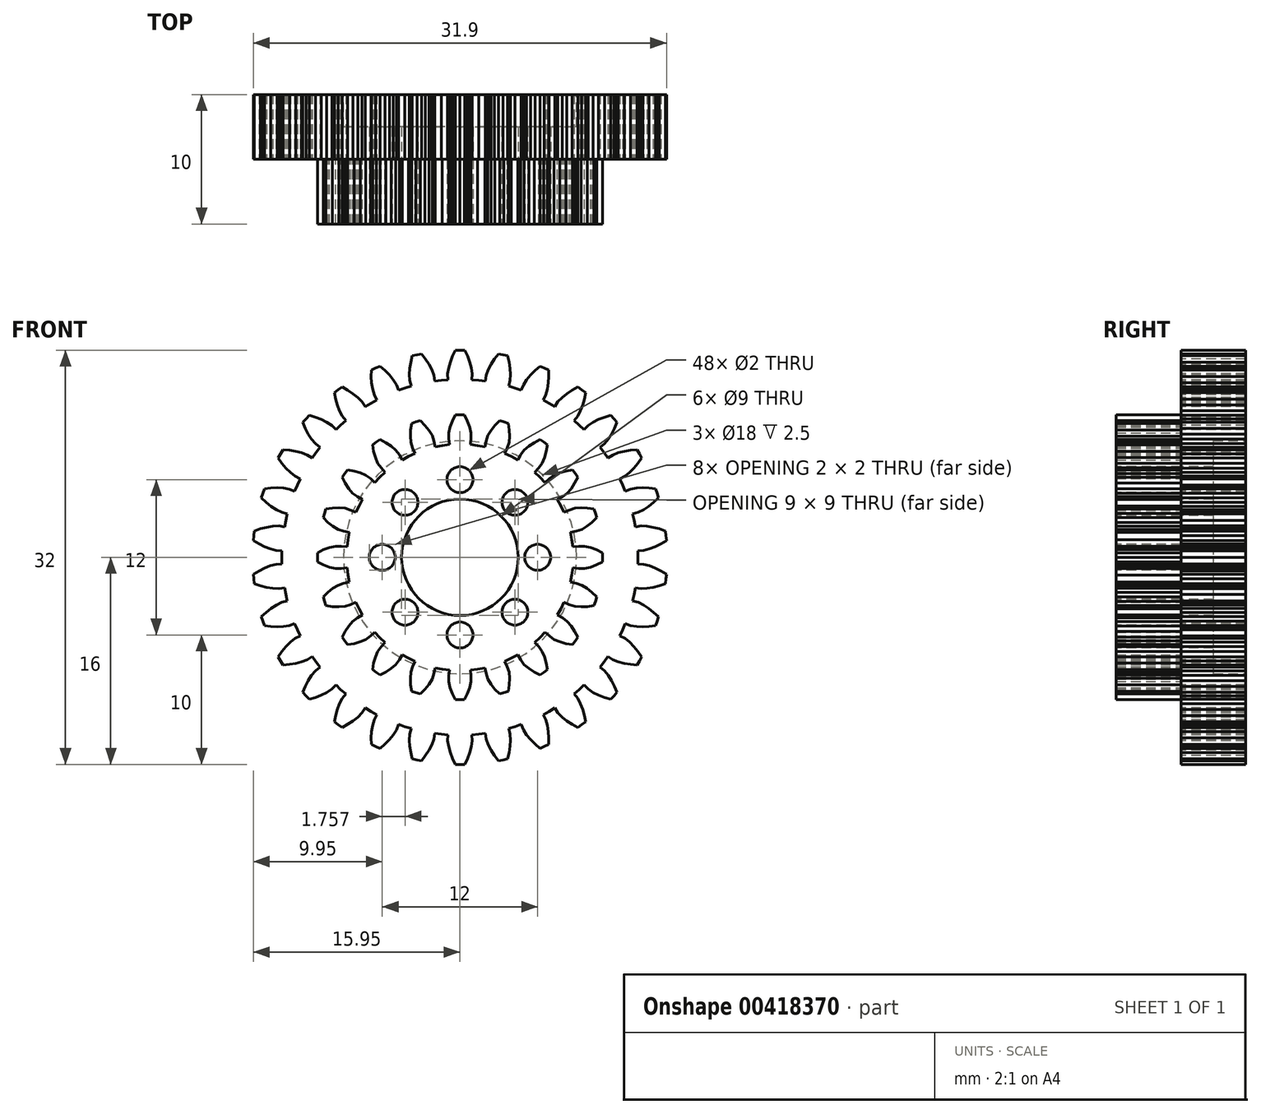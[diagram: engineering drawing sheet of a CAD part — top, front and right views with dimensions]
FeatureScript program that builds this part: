
annotation { "Feature Type Name" : "Feature", "Feature Type Description" : "" }
export const myFeature = defineFeature(function(context is Context, id is Id, definition is map)
    precondition{}
    {
        {
            var Q0;
            Q0=qCreatedBy(makeId("Front.planeOp"),FACE);
            var sketch = newSketch(context, id + "F0", { "sketchPlane" : qUnion([Q0])});
            skLineSegment(sketch, "E0", {"start": v(8.64, -1.37) * mm, "end": v(8.71, -0.82) * mm});
            skLineSegment(sketch, "E1", {"start": v(8.71, -0.82) * mm, "end": v(9.16, -0.86) * mm});
            skLineSegment(sketch, "E2", {"start": v(9.16, -0.86) * mm, "end": v(9.61, -0.86) * mm});
            skLineSegment(sketch, "E3", {"start": v(9.61, -0.86) * mm, "end": v(10.07, -0.75) * mm});
            skLineSegment(sketch, "E4", {"start": v(10.07, -0.75) * mm, "end": v(10.53, -0.58) * mm});
            skLineSegment(sketch, "E5", {"start": v(10.53, -0.58) * mm, "end": v(11, -0.35) * mm});
            skLineSegment(sketch, "E6", {"start": v(11, -0.35) * mm, "end": v(11, 0) * mm});
            skLineSegment(sketch, "E7", {"start": v(11, 0) * mm, "end": v(11, 0.35) * mm});
            skLineSegment(sketch, "E8", {"start": v(11, 0.35) * mm, "end": v(10.53, 0.58) * mm});
            skLineSegment(sketch, "E9", {"start": v(10.53, 0.58) * mm, "end": v(10.07, 0.75) * mm});
            skLineSegment(sketch, "E10", {"start": v(10.07, 0.75) * mm, "end": v(9.61, 0.86) * mm});
            skLineSegment(sketch, "E11", {"start": v(9.61, 0.86) * mm, "end": v(9.16, 0.86) * mm});
            skLineSegment(sketch, "E12", {"start": v(9.16, 0.86) * mm, "end": v(8.71, 0.82) * mm});
            skLineSegment(sketch, "E13", {"start": v(8.71, 0.82) * mm, "end": v(8.64, 1.37) * mm});
            skLineSegment(sketch, "E14", {"start": v(8.64, 1.37) * mm, "end": v(8.54, 1.92) * mm});
            skLineSegment(sketch, "E15", {"start": v(8.54, 1.92) * mm, "end": v(8.98, 2.01) * mm});
            skLineSegment(sketch, "E16", {"start": v(8.98, 2.01) * mm, "end": v(9.4, 2.15) * mm});
            skLineSegment(sketch, "E17", {"start": v(9.4, 2.15) * mm, "end": v(9.81, 2.4) * mm});
            skLineSegment(sketch, "E18", {"start": v(9.81, 2.4) * mm, "end": v(10.2, 2.7) * mm});
            skLineSegment(sketch, "E19", {"start": v(10.2, 2.7) * mm, "end": v(10.56, 3.07) * mm});
            skLineSegment(sketch, "E20", {"start": v(10.56, 3.07) * mm, "end": v(10.46, 3.4) * mm});
            skLineSegment(sketch, "E21", {"start": v(10.46, 3.4) * mm, "end": v(10.35, 3.73) * mm});
            skLineSegment(sketch, "E22", {"start": v(10.35, 3.73) * mm, "end": v(9.84, 3.8) * mm});
            skLineSegment(sketch, "E23", {"start": v(9.84, 3.8) * mm, "end": v(9.35, 3.83) * mm});
            skLineSegment(sketch, "E24", {"start": v(9.35, 3.83) * mm, "end": v(8.88, 3.79) * mm});
            skLineSegment(sketch, "E25", {"start": v(8.88, 3.79) * mm, "end": v(8.45, 3.65) * mm});
            skLineSegment(sketch, "E26", {"start": v(8.45, 3.65) * mm, "end": v(8.03, 3.47) * mm});
            skLineSegment(sketch, "E27", {"start": v(8.03, 3.47) * mm, "end": v(7.8, 3.97) * mm});
            skLineSegment(sketch, "E28", {"start": v(7.8, 3.97) * mm, "end": v(7.53, 4.46) * mm});
            skLineSegment(sketch, "E29", {"start": v(7.53, 4.46) * mm, "end": v(7.92, 4.69) * mm});
            skLineSegment(sketch, "E30", {"start": v(7.92, 4.69) * mm, "end": v(8.28, 4.95) * mm});
            skLineSegment(sketch, "E31", {"start": v(8.28, 4.95) * mm, "end": v(8.6, 5.3) * mm});
            skLineSegment(sketch, "E32", {"start": v(8.6, 5.3) * mm, "end": v(8.86, 5.72) * mm});
            skLineSegment(sketch, "E33", {"start": v(8.86, 5.72) * mm, "end": v(9.1, 6.18) * mm});
            skLineSegment(sketch, "E34", {"start": v(9.1, 6.18) * mm, "end": v(8.9, 6.47) * mm});
            skLineSegment(sketch, "E35", {"start": v(8.9, 6.47) * mm, "end": v(8.7, 6.74) * mm});
            skLineSegment(sketch, "E36", {"start": v(8.7, 6.74) * mm, "end": v(8.18, 6.66) * mm});
            skLineSegment(sketch, "E37", {"start": v(8.18, 6.66) * mm, "end": v(7.7, 6.53) * mm});
            skLineSegment(sketch, "E38", {"start": v(7.7, 6.53) * mm, "end": v(7.27, 6.35) * mm});
            skLineSegment(sketch, "E39", {"start": v(7.27, 6.35) * mm, "end": v(6.9, 6.08) * mm});
            skLineSegment(sketch, "E40", {"start": v(6.9, 6.08) * mm, "end": v(6.57, 5.78) * mm});
            skLineSegment(sketch, "E41", {"start": v(6.57, 5.78) * mm, "end": v(6.19, 6.19) * mm});
            skLineSegment(sketch, "E42", {"start": v(6.19, 6.19) * mm, "end": v(5.78, 6.57) * mm});
            skLineSegment(sketch, "E43", {"start": v(5.78, 6.57) * mm, "end": v(6.08, 6.9) * mm});
            skLineSegment(sketch, "E44", {"start": v(6.08, 6.9) * mm, "end": v(6.35, 7.27) * mm});
            skLineSegment(sketch, "E45", {"start": v(6.35, 7.27) * mm, "end": v(6.53, 7.7) * mm});
            skLineSegment(sketch, "E46", {"start": v(6.53, 7.7) * mm, "end": v(6.66, 8.18) * mm});
            skLineSegment(sketch, "E47", {"start": v(6.66, 8.18) * mm, "end": v(6.74, 8.7) * mm});
            skLineSegment(sketch, "E48", {"start": v(6.74, 8.7) * mm, "end": v(6.47, 8.9) * mm});
            skLineSegment(sketch, "E49", {"start": v(6.47, 8.9) * mm, "end": v(6.18, 9.1) * mm});
            skLineSegment(sketch, "E50", {"start": v(6.18, 9.1) * mm, "end": v(5.72, 8.86) * mm});
            skLineSegment(sketch, "E51", {"start": v(5.72, 8.86) * mm, "end": v(5.3, 8.6) * mm});
            skLineSegment(sketch, "E52", {"start": v(5.3, 8.6) * mm, "end": v(4.95, 8.28) * mm});
            skLineSegment(sketch, "E53", {"start": v(4.95, 8.28) * mm, "end": v(4.69, 7.92) * mm});
            skLineSegment(sketch, "E54", {"start": v(4.69, 7.92) * mm, "end": v(4.46, 7.53) * mm});
            skLineSegment(sketch, "E55", {"start": v(4.46, 7.53) * mm, "end": v(3.97, 7.8) * mm});
            skLineSegment(sketch, "E56", {"start": v(3.97, 7.8) * mm, "end": v(3.47, 8.03) * mm});
            skLineSegment(sketch, "E57", {"start": v(3.47, 8.03) * mm, "end": v(3.65, 8.45) * mm});
            skLineSegment(sketch, "E58", {"start": v(3.65, 8.45) * mm, "end": v(3.79, 8.88) * mm});
            skLineSegment(sketch, "E59", {"start": v(3.79, 8.88) * mm, "end": v(3.83, 9.35) * mm});
            skLineSegment(sketch, "E60", {"start": v(3.83, 9.35) * mm, "end": v(3.8, 9.84) * mm});
            skLineSegment(sketch, "E61", {"start": v(3.8, 9.84) * mm, "end": v(3.73, 10.35) * mm});
            skLineSegment(sketch, "E62", {"start": v(3.73, 10.35) * mm, "end": v(3.4, 10.46) * mm});
            skLineSegment(sketch, "E63", {"start": v(3.4, 10.46) * mm, "end": v(3.07, 10.56) * mm});
            skLineSegment(sketch, "E64", {"start": v(3.07, 10.56) * mm, "end": v(2.7, 10.2) * mm});
            skLineSegment(sketch, "E65", {"start": v(2.7, 10.2) * mm, "end": v(2.4, 9.81) * mm});
            skLineSegment(sketch, "E66", {"start": v(2.4, 9.81) * mm, "end": v(2.15, 9.4) * mm});
            skLineSegment(sketch, "E67", {"start": v(2.15, 9.4) * mm, "end": v(2.01, 8.98) * mm});
            skLineSegment(sketch, "E68", {"start": v(2.01, 8.98) * mm, "end": v(1.92, 8.54) * mm});
            skLineSegment(sketch, "E69", {"start": v(1.92, 8.54) * mm, "end": v(1.37, 8.64) * mm});
            skLineSegment(sketch, "E70", {"start": v(1.37, 8.64) * mm, "end": v(0.82, 8.71) * mm});
            skLineSegment(sketch, "E71", {"start": v(0.82, 8.71) * mm, "end": v(0.86, 9.16) * mm});
            skLineSegment(sketch, "E72", {"start": v(0.86, 9.16) * mm, "end": v(0.86, 9.61) * mm});
            skLineSegment(sketch, "E73", {"start": v(0.86, 9.61) * mm, "end": v(0.75, 10.07) * mm});
            skLineSegment(sketch, "E74", {"start": v(0.75, 10.07) * mm, "end": v(0.58, 10.53) * mm});
            skLineSegment(sketch, "E75", {"start": v(0.58, 10.53) * mm, "end": v(0.35, 11) * mm});
            skLineSegment(sketch, "E76", {"start": v(0.35, 11) * mm, "end": v(0, 11) * mm});
            skLineSegment(sketch, "E77", {"start": v(0, 11) * mm, "end": v(-0.35, 11) * mm});
            skLineSegment(sketch, "E78", {"start": v(-0.35, 11) * mm, "end": v(-0.58, 10.53) * mm});
            skLineSegment(sketch, "E79", {"start": v(-0.58, 10.53) * mm, "end": v(-0.75, 10.07) * mm});
            skLineSegment(sketch, "E80", {"start": v(-0.75, 10.07) * mm, "end": v(-0.86, 9.61) * mm});
            skLineSegment(sketch, "E81", {"start": v(-0.86, 9.61) * mm, "end": v(-0.86, 9.16) * mm});
            skLineSegment(sketch, "E82", {"start": v(-0.86, 9.16) * mm, "end": v(-0.82, 8.71) * mm});
            skLineSegment(sketch, "E83", {"start": v(-0.82, 8.71) * mm, "end": v(-1.37, 8.64) * mm});
            skLineSegment(sketch, "E84", {"start": v(-1.37, 8.64) * mm, "end": v(-1.92, 8.54) * mm});
            skLineSegment(sketch, "E85", {"start": v(-1.92, 8.54) * mm, "end": v(-2.01, 8.98) * mm});
            skLineSegment(sketch, "E86", {"start": v(-2.01, 8.98) * mm, "end": v(-2.15, 9.4) * mm});
            skLineSegment(sketch, "E87", {"start": v(-2.15, 9.4) * mm, "end": v(-2.4, 9.81) * mm});
            skLineSegment(sketch, "E88", {"start": v(-2.4, 9.81) * mm, "end": v(-2.7, 10.2) * mm});
            skLineSegment(sketch, "E89", {"start": v(-2.7, 10.2) * mm, "end": v(-3.07, 10.56) * mm});
            skLineSegment(sketch, "E90", {"start": v(-3.07, 10.56) * mm, "end": v(-3.4, 10.46) * mm});
            skLineSegment(sketch, "E91", {"start": v(-3.4, 10.46) * mm, "end": v(-3.73, 10.35) * mm});
            skLineSegment(sketch, "E92", {"start": v(-3.73, 10.35) * mm, "end": v(-3.8, 9.84) * mm});
            skLineSegment(sketch, "E93", {"start": v(-3.8, 9.84) * mm, "end": v(-3.83, 9.35) * mm});
            skLineSegment(sketch, "E94", {"start": v(-3.83, 9.35) * mm, "end": v(-3.79, 8.88) * mm});
            skLineSegment(sketch, "E95", {"start": v(-3.79, 8.88) * mm, "end": v(-3.65, 8.45) * mm});
            skLineSegment(sketch, "E96", {"start": v(-3.65, 8.45) * mm, "end": v(-3.47, 8.03) * mm});
            skLineSegment(sketch, "E97", {"start": v(-3.47, 8.03) * mm, "end": v(-3.97, 7.8) * mm});
            skLineSegment(sketch, "E98", {"start": v(-3.97, 7.8) * mm, "end": v(-4.46, 7.53) * mm});
            skLineSegment(sketch, "E99", {"start": v(-4.46, 7.53) * mm, "end": v(-4.69, 7.92) * mm});
            skLineSegment(sketch, "E100", {"start": v(-4.69, 7.92) * mm, "end": v(-4.95, 8.28) * mm});
            skLineSegment(sketch, "E101", {"start": v(-4.95, 8.28) * mm, "end": v(-5.3, 8.6) * mm});
            skLineSegment(sketch, "E102", {"start": v(-5.3, 8.6) * mm, "end": v(-5.72, 8.86) * mm});
            skLineSegment(sketch, "E103", {"start": v(-5.72, 8.86) * mm, "end": v(-6.18, 9.1) * mm});
            skLineSegment(sketch, "E104", {"start": v(-6.18, 9.1) * mm, "end": v(-6.47, 8.9) * mm});
            skLineSegment(sketch, "E105", {"start": v(-6.47, 8.9) * mm, "end": v(-6.74, 8.7) * mm});
            skLineSegment(sketch, "E106", {"start": v(-6.74, 8.7) * mm, "end": v(-6.66, 8.18) * mm});
            skLineSegment(sketch, "E107", {"start": v(-6.66, 8.18) * mm, "end": v(-6.53, 7.7) * mm});
            skLineSegment(sketch, "E108", {"start": v(-6.53, 7.7) * mm, "end": v(-6.35, 7.27) * mm});
            skLineSegment(sketch, "E109", {"start": v(-6.35, 7.27) * mm, "end": v(-6.08, 6.9) * mm});
            skLineSegment(sketch, "E110", {"start": v(-6.08, 6.9) * mm, "end": v(-5.78, 6.57) * mm});
            skLineSegment(sketch, "E111", {"start": v(-5.78, 6.57) * mm, "end": v(-6.19, 6.19) * mm});
            skLineSegment(sketch, "E112", {"start": v(-6.19, 6.19) * mm, "end": v(-6.57, 5.78) * mm});
            skLineSegment(sketch, "E113", {"start": v(-6.57, 5.78) * mm, "end": v(-6.9, 6.08) * mm});
            skLineSegment(sketch, "E114", {"start": v(-6.9, 6.08) * mm, "end": v(-7.27, 6.35) * mm});
            skLineSegment(sketch, "E115", {"start": v(-7.27, 6.35) * mm, "end": v(-7.7, 6.53) * mm});
            skLineSegment(sketch, "E116", {"start": v(-7.7, 6.53) * mm, "end": v(-8.18, 6.66) * mm});
            skLineSegment(sketch, "E117", {"start": v(-8.18, 6.66) * mm, "end": v(-8.7, 6.74) * mm});
            skLineSegment(sketch, "E118", {"start": v(-8.7, 6.74) * mm, "end": v(-8.9, 6.47) * mm});
            skLineSegment(sketch, "E119", {"start": v(-8.9, 6.47) * mm, "end": v(-9.1, 6.18) * mm});
            skLineSegment(sketch, "E120", {"start": v(-9.1, 6.18) * mm, "end": v(-8.86, 5.72) * mm});
            skLineSegment(sketch, "E121", {"start": v(-8.86, 5.72) * mm, "end": v(-8.6, 5.3) * mm});
            skLineSegment(sketch, "E122", {"start": v(-8.6, 5.3) * mm, "end": v(-8.28, 4.95) * mm});
            skLineSegment(sketch, "E123", {"start": v(-8.28, 4.95) * mm, "end": v(-7.92, 4.69) * mm});
            skLineSegment(sketch, "E124", {"start": v(-7.92, 4.69) * mm, "end": v(-7.53, 4.46) * mm});
            skLineSegment(sketch, "E125", {"start": v(-7.53, 4.46) * mm, "end": v(-7.8, 3.97) * mm});
            skLineSegment(sketch, "E126", {"start": v(-7.8, 3.97) * mm, "end": v(-8.03, 3.47) * mm});
            skLineSegment(sketch, "E127", {"start": v(-8.03, 3.47) * mm, "end": v(-8.45, 3.65) * mm});
            skLineSegment(sketch, "E128", {"start": v(-8.45, 3.65) * mm, "end": v(-8.88, 3.79) * mm});
            skLineSegment(sketch, "E129", {"start": v(-8.88, 3.79) * mm, "end": v(-9.35, 3.83) * mm});
            skLineSegment(sketch, "E130", {"start": v(-9.35, 3.83) * mm, "end": v(-9.84, 3.8) * mm});
            skLineSegment(sketch, "E131", {"start": v(-9.84, 3.8) * mm, "end": v(-10.35, 3.73) * mm});
            skLineSegment(sketch, "E132", {"start": v(-10.35, 3.73) * mm, "end": v(-10.46, 3.4) * mm});
            skLineSegment(sketch, "E133", {"start": v(-10.46, 3.4) * mm, "end": v(-10.56, 3.07) * mm});
            skLineSegment(sketch, "E134", {"start": v(-10.56, 3.07) * mm, "end": v(-10.2, 2.7) * mm});
            skLineSegment(sketch, "E135", {"start": v(-10.2, 2.7) * mm, "end": v(-9.81, 2.4) * mm});
            skLineSegment(sketch, "E136", {"start": v(-9.81, 2.4) * mm, "end": v(-9.4, 2.15) * mm});
            skLineSegment(sketch, "E137", {"start": v(-9.4, 2.15) * mm, "end": v(-8.98, 2.01) * mm});
            skLineSegment(sketch, "E138", {"start": v(-8.98, 2.01) * mm, "end": v(-8.54, 1.92) * mm});
            skLineSegment(sketch, "E139", {"start": v(-8.54, 1.92) * mm, "end": v(-8.64, 1.37) * mm});
            skLineSegment(sketch, "E140", {"start": v(-8.64, 1.37) * mm, "end": v(-8.71, 0.82) * mm});
            skLineSegment(sketch, "E141", {"start": v(-8.71, 0.82) * mm, "end": v(-9.16, 0.86) * mm});
            skLineSegment(sketch, "E142", {"start": v(-9.16, 0.86) * mm, "end": v(-9.61, 0.86) * mm});
            skLineSegment(sketch, "E143", {"start": v(-9.61, 0.86) * mm, "end": v(-10.07, 0.75) * mm});
            skLineSegment(sketch, "E144", {"start": v(-10.07, 0.75) * mm, "end": v(-10.53, 0.58) * mm});
            skLineSegment(sketch, "E145", {"start": v(-10.53, 0.58) * mm, "end": v(-11, 0.35) * mm});
            skLineSegment(sketch, "E146", {"start": v(-11, 0.35) * mm, "end": v(-11, 0) * mm});
            skLineSegment(sketch, "E147", {"start": v(-11, 0) * mm, "end": v(-11, -0.35) * mm});
            skLineSegment(sketch, "E148", {"start": v(-11, -0.35) * mm, "end": v(-10.53, -0.58) * mm});
            skLineSegment(sketch, "E149", {"start": v(-10.53, -0.58) * mm, "end": v(-10.07, -0.75) * mm});
            skLineSegment(sketch, "E150", {"start": v(-10.07, -0.75) * mm, "end": v(-9.61, -0.86) * mm});
            skLineSegment(sketch, "E151", {"start": v(-9.61, -0.86) * mm, "end": v(-9.16, -0.86) * mm});
            skLineSegment(sketch, "E152", {"start": v(-9.16, -0.86) * mm, "end": v(-8.71, -0.82) * mm});
            skLineSegment(sketch, "E153", {"start": v(-8.71, -0.82) * mm, "end": v(-8.64, -1.37) * mm});
            skLineSegment(sketch, "E154", {"start": v(-8.64, -1.37) * mm, "end": v(-8.54, -1.92) * mm});
            skLineSegment(sketch, "E155", {"start": v(-8.54, -1.92) * mm, "end": v(-8.98, -2.01) * mm});
            skLineSegment(sketch, "E156", {"start": v(-8.98, -2.01) * mm, "end": v(-9.4, -2.15) * mm});
            skLineSegment(sketch, "E157", {"start": v(-9.4, -2.15) * mm, "end": v(-9.81, -2.4) * mm});
            skLineSegment(sketch, "E158", {"start": v(-9.81, -2.4) * mm, "end": v(-10.2, -2.7) * mm});
            skLineSegment(sketch, "E159", {"start": v(-10.2, -2.7) * mm, "end": v(-10.56, -3.07) * mm});
            skLineSegment(sketch, "E160", {"start": v(-10.56, -3.07) * mm, "end": v(-10.46, -3.4) * mm});
            skLineSegment(sketch, "E161", {"start": v(-10.46, -3.4) * mm, "end": v(-10.35, -3.73) * mm});
            skLineSegment(sketch, "E162", {"start": v(-10.35, -3.73) * mm, "end": v(-9.84, -3.8) * mm});
            skLineSegment(sketch, "E163", {"start": v(-9.84, -3.8) * mm, "end": v(-9.35, -3.83) * mm});
            skLineSegment(sketch, "E164", {"start": v(-9.35, -3.83) * mm, "end": v(-8.88, -3.79) * mm});
            skLineSegment(sketch, "E165", {"start": v(-8.88, -3.79) * mm, "end": v(-8.45, -3.65) * mm});
            skLineSegment(sketch, "E166", {"start": v(-8.45, -3.65) * mm, "end": v(-8.03, -3.47) * mm});
            skLineSegment(sketch, "E167", {"start": v(-8.03, -3.47) * mm, "end": v(-7.8, -3.97) * mm});
            skLineSegment(sketch, "E168", {"start": v(-7.8, -3.97) * mm, "end": v(-7.53, -4.46) * mm});
            skLineSegment(sketch, "E169", {"start": v(-7.53, -4.46) * mm, "end": v(-7.92, -4.69) * mm});
            skLineSegment(sketch, "E170", {"start": v(-7.92, -4.69) * mm, "end": v(-8.28, -4.95) * mm});
            skLineSegment(sketch, "E171", {"start": v(-8.28, -4.95) * mm, "end": v(-8.6, -5.3) * mm});
            skLineSegment(sketch, "E172", {"start": v(-8.6, -5.3) * mm, "end": v(-8.86, -5.72) * mm});
            skLineSegment(sketch, "E173", {"start": v(-8.86, -5.72) * mm, "end": v(-9.1, -6.18) * mm});
            skLineSegment(sketch, "E174", {"start": v(-9.1, -6.18) * mm, "end": v(-8.9, -6.47) * mm});
            skLineSegment(sketch, "E175", {"start": v(-8.9, -6.47) * mm, "end": v(-8.7, -6.74) * mm});
            skLineSegment(sketch, "E176", {"start": v(-8.7, -6.74) * mm, "end": v(-8.18, -6.66) * mm});
            skLineSegment(sketch, "E177", {"start": v(-8.18, -6.66) * mm, "end": v(-7.7, -6.53) * mm});
            skLineSegment(sketch, "E178", {"start": v(-7.7, -6.53) * mm, "end": v(-7.27, -6.35) * mm});
            skLineSegment(sketch, "E179", {"start": v(-7.27, -6.35) * mm, "end": v(-6.9, -6.08) * mm});
            skLineSegment(sketch, "E180", {"start": v(-6.9, -6.08) * mm, "end": v(-6.57, -5.78) * mm});
            skLineSegment(sketch, "E181", {"start": v(-6.57, -5.78) * mm, "end": v(-6.19, -6.19) * mm});
            skLineSegment(sketch, "E182", {"start": v(-6.19, -6.19) * mm, "end": v(-5.78, -6.57) * mm});
            skLineSegment(sketch, "E183", {"start": v(-5.78, -6.57) * mm, "end": v(-6.08, -6.9) * mm});
            skLineSegment(sketch, "E184", {"start": v(-6.08, -6.9) * mm, "end": v(-6.35, -7.27) * mm});
            skLineSegment(sketch, "E185", {"start": v(-6.35, -7.27) * mm, "end": v(-6.53, -7.7) * mm});
            skLineSegment(sketch, "E186", {"start": v(-6.53, -7.7) * mm, "end": v(-6.66, -8.18) * mm});
            skLineSegment(sketch, "E187", {"start": v(-6.66, -8.18) * mm, "end": v(-6.74, -8.7) * mm});
            skLineSegment(sketch, "E188", {"start": v(-6.74, -8.7) * mm, "end": v(-6.47, -8.9) * mm});
            skLineSegment(sketch, "E189", {"start": v(-6.47, -8.9) * mm, "end": v(-6.18, -9.1) * mm});
            skLineSegment(sketch, "E190", {"start": v(-6.18, -9.1) * mm, "end": v(-5.72, -8.86) * mm});
            skLineSegment(sketch, "E191", {"start": v(-5.72, -8.86) * mm, "end": v(-5.3, -8.6) * mm});
            skLineSegment(sketch, "E192", {"start": v(-5.3, -8.6) * mm, "end": v(-4.95, -8.28) * mm});
            skLineSegment(sketch, "E193", {"start": v(-4.95, -8.28) * mm, "end": v(-4.69, -7.92) * mm});
            skLineSegment(sketch, "E194", {"start": v(-4.69, -7.92) * mm, "end": v(-4.46, -7.53) * mm});
            skLineSegment(sketch, "E195", {"start": v(-4.46, -7.53) * mm, "end": v(-3.97, -7.8) * mm});
            skLineSegment(sketch, "E196", {"start": v(-3.97, -7.8) * mm, "end": v(-3.47, -8.03) * mm});
            skLineSegment(sketch, "E197", {"start": v(-3.47, -8.03) * mm, "end": v(-3.65, -8.45) * mm});
            skLineSegment(sketch, "E198", {"start": v(-3.65, -8.45) * mm, "end": v(-3.79, -8.88) * mm});
            skLineSegment(sketch, "E199", {"start": v(-3.79, -8.88) * mm, "end": v(-3.83, -9.35) * mm});
            skLineSegment(sketch, "E200", {"start": v(-3.83, -9.35) * mm, "end": v(-3.8, -9.84) * mm});
            skLineSegment(sketch, "E201", {"start": v(-3.8, -9.84) * mm, "end": v(-3.73, -10.35) * mm});
            skLineSegment(sketch, "E202", {"start": v(-3.73, -10.35) * mm, "end": v(-3.4, -10.46) * mm});
            skLineSegment(sketch, "E203", {"start": v(-3.4, -10.46) * mm, "end": v(-3.07, -10.56) * mm});
            skLineSegment(sketch, "E204", {"start": v(-3.07, -10.56) * mm, "end": v(-2.7, -10.2) * mm});
            skLineSegment(sketch, "E205", {"start": v(-2.7, -10.2) * mm, "end": v(-2.4, -9.81) * mm});
            skLineSegment(sketch, "E206", {"start": v(-2.4, -9.81) * mm, "end": v(-2.15, -9.4) * mm});
            skLineSegment(sketch, "E207", {"start": v(-2.15, -9.4) * mm, "end": v(-2.01, -8.98) * mm});
            skLineSegment(sketch, "E208", {"start": v(-2.01, -8.98) * mm, "end": v(-1.92, -8.54) * mm});
            skLineSegment(sketch, "E209", {"start": v(-1.92, -8.54) * mm, "end": v(-1.37, -8.64) * mm});
            skLineSegment(sketch, "E210", {"start": v(-1.37, -8.64) * mm, "end": v(-0.82, -8.71) * mm});
            skLineSegment(sketch, "E211", {"start": v(-0.82, -8.71) * mm, "end": v(-0.86, -9.16) * mm});
            skLineSegment(sketch, "E212", {"start": v(-0.86, -9.16) * mm, "end": v(-0.86, -9.61) * mm});
            skLineSegment(sketch, "E213", {"start": v(-0.86, -9.61) * mm, "end": v(-0.75, -10.07) * mm});
            skLineSegment(sketch, "E214", {"start": v(-0.75, -10.07) * mm, "end": v(-0.58, -10.53) * mm});
            skLineSegment(sketch, "E215", {"start": v(-0.58, -10.53) * mm, "end": v(-0.35, -11) * mm});
            skLineSegment(sketch, "E216", {"start": v(-0.35, -11) * mm, "end": v(0, -11) * mm});
            skLineSegment(sketch, "E217", {"start": v(0, -11) * mm, "end": v(0.35, -11) * mm});
            skLineSegment(sketch, "E218", {"start": v(0.35, -11) * mm, "end": v(0.58, -10.53) * mm});
            skLineSegment(sketch, "E219", {"start": v(0.58, -10.53) * mm, "end": v(0.75, -10.07) * mm});
            skLineSegment(sketch, "E220", {"start": v(0.75, -10.07) * mm, "end": v(0.86, -9.61) * mm});
            skLineSegment(sketch, "E221", {"start": v(0.86, -9.61) * mm, "end": v(0.86, -9.16) * mm});
            skLineSegment(sketch, "E222", {"start": v(0.86, -9.16) * mm, "end": v(0.82, -8.71) * mm});
            skLineSegment(sketch, "E223", {"start": v(0.82, -8.71) * mm, "end": v(1.37, -8.64) * mm});
            skLineSegment(sketch, "E224", {"start": v(1.37, -8.64) * mm, "end": v(1.92, -8.54) * mm});
            skLineSegment(sketch, "E225", {"start": v(1.92, -8.54) * mm, "end": v(2.01, -8.98) * mm});
            skLineSegment(sketch, "E226", {"start": v(2.01, -8.98) * mm, "end": v(2.15, -9.4) * mm});
            skLineSegment(sketch, "E227", {"start": v(2.15, -9.4) * mm, "end": v(2.4, -9.81) * mm});
            skLineSegment(sketch, "E228", {"start": v(2.4, -9.81) * mm, "end": v(2.7, -10.2) * mm});
            skLineSegment(sketch, "E229", {"start": v(2.7, -10.2) * mm, "end": v(3.07, -10.56) * mm});
            skLineSegment(sketch, "E230", {"start": v(3.07, -10.56) * mm, "end": v(3.4, -10.46) * mm});
            skLineSegment(sketch, "E231", {"start": v(3.4, -10.46) * mm, "end": v(3.73, -10.35) * mm});
            skLineSegment(sketch, "E232", {"start": v(3.73, -10.35) * mm, "end": v(3.8, -9.84) * mm});
            skLineSegment(sketch, "E233", {"start": v(3.8, -9.84) * mm, "end": v(3.83, -9.35) * mm});
            skLineSegment(sketch, "E234", {"start": v(3.83, -9.35) * mm, "end": v(3.79, -8.88) * mm});
            skLineSegment(sketch, "E235", {"start": v(3.79, -8.88) * mm, "end": v(3.65, -8.45) * mm});
            skLineSegment(sketch, "E236", {"start": v(3.65, -8.45) * mm, "end": v(3.47, -8.03) * mm});
            skLineSegment(sketch, "E237", {"start": v(3.47, -8.03) * mm, "end": v(3.97, -7.8) * mm});
            skLineSegment(sketch, "E238", {"start": v(3.97, -7.8) * mm, "end": v(4.46, -7.53) * mm});
            skLineSegment(sketch, "E239", {"start": v(4.46, -7.53) * mm, "end": v(4.69, -7.92) * mm});
            skLineSegment(sketch, "E240", {"start": v(4.69, -7.92) * mm, "end": v(4.95, -8.28) * mm});
            skLineSegment(sketch, "E241", {"start": v(4.95, -8.28) * mm, "end": v(5.3, -8.6) * mm});
            skLineSegment(sketch, "E242", {"start": v(5.3, -8.6) * mm, "end": v(5.72, -8.86) * mm});
            skLineSegment(sketch, "E243", {"start": v(5.72, -8.86) * mm, "end": v(6.18, -9.1) * mm});
            skLineSegment(sketch, "E244", {"start": v(6.18, -9.1) * mm, "end": v(6.47, -8.9) * mm});
            skLineSegment(sketch, "E245", {"start": v(6.47, -8.9) * mm, "end": v(6.74, -8.7) * mm});
            skLineSegment(sketch, "E246", {"start": v(6.74, -8.7) * mm, "end": v(6.66, -8.18) * mm});
            skLineSegment(sketch, "E247", {"start": v(6.66, -8.18) * mm, "end": v(6.53, -7.7) * mm});
            skLineSegment(sketch, "E248", {"start": v(6.53, -7.7) * mm, "end": v(6.35, -7.27) * mm});
            skLineSegment(sketch, "E249", {"start": v(6.35, -7.27) * mm, "end": v(6.08, -6.9) * mm});
            skLineSegment(sketch, "E250", {"start": v(6.08, -6.9) * mm, "end": v(5.78, -6.57) * mm});
            skLineSegment(sketch, "E251", {"start": v(5.78, -6.57) * mm, "end": v(6.19, -6.19) * mm});
            skLineSegment(sketch, "E252", {"start": v(6.19, -6.19) * mm, "end": v(6.57, -5.78) * mm});
            skLineSegment(sketch, "E253", {"start": v(6.57, -5.78) * mm, "end": v(6.9, -6.08) * mm});
            skLineSegment(sketch, "E254", {"start": v(6.9, -6.08) * mm, "end": v(7.27, -6.35) * mm});
            skLineSegment(sketch, "E255", {"start": v(7.27, -6.35) * mm, "end": v(7.7, -6.53) * mm});
            skLineSegment(sketch, "E256", {"start": v(7.7, -6.53) * mm, "end": v(8.18, -6.66) * mm});
            skLineSegment(sketch, "E257", {"start": v(8.18, -6.66) * mm, "end": v(8.7, -6.74) * mm});
            skLineSegment(sketch, "E258", {"start": v(8.7, -6.74) * mm, "end": v(8.9, -6.47) * mm});
            skLineSegment(sketch, "E259", {"start": v(8.9, -6.47) * mm, "end": v(9.1, -6.18) * mm});
            skLineSegment(sketch, "E260", {"start": v(9.1, -6.18) * mm, "end": v(8.86, -5.72) * mm});
            skLineSegment(sketch, "E261", {"start": v(8.86, -5.72) * mm, "end": v(8.6, -5.3) * mm});
            skLineSegment(sketch, "E262", {"start": v(8.6, -5.3) * mm, "end": v(8.28, -4.95) * mm});
            skLineSegment(sketch, "E263", {"start": v(8.28, -4.95) * mm, "end": v(7.92, -4.69) * mm});
            skLineSegment(sketch, "E264", {"start": v(7.92, -4.69) * mm, "end": v(7.53, -4.46) * mm});
            skLineSegment(sketch, "E265", {"start": v(7.53, -4.46) * mm, "end": v(7.8, -3.97) * mm});
            skLineSegment(sketch, "E266", {"start": v(7.8, -3.97) * mm, "end": v(8.03, -3.47) * mm});
            skLineSegment(sketch, "E267", {"start": v(8.03, -3.47) * mm, "end": v(8.45, -3.65) * mm});
            skLineSegment(sketch, "E268", {"start": v(8.45, -3.65) * mm, "end": v(8.88, -3.79) * mm});
            skLineSegment(sketch, "E269", {"start": v(8.88, -3.79) * mm, "end": v(9.35, -3.83) * mm});
            skLineSegment(sketch, "E270", {"start": v(9.35, -3.83) * mm, "end": v(9.84, -3.8) * mm});
            skLineSegment(sketch, "E271", {"start": v(9.84, -3.8) * mm, "end": v(10.35, -3.73) * mm});
            skLineSegment(sketch, "E272", {"start": v(10.35, -3.73) * mm, "end": v(10.46, -3.4) * mm});
            skLineSegment(sketch, "E273", {"start": v(10.46, -3.4) * mm, "end": v(10.56, -3.07) * mm});
            skLineSegment(sketch, "E274", {"start": v(10.56, -3.07) * mm, "end": v(10.2, -2.7) * mm});
            skLineSegment(sketch, "E275", {"start": v(10.2, -2.7) * mm, "end": v(9.81, -2.4) * mm});
            skLineSegment(sketch, "E276", {"start": v(9.81, -2.4) * mm, "end": v(9.4, -2.15) * mm});
            skLineSegment(sketch, "E277", {"start": v(9.4, -2.15) * mm, "end": v(8.98, -2.01) * mm});
            skLineSegment(sketch, "E278", {"start": v(8.98, -2.01) * mm, "end": v(8.54, -1.92) * mm});
            skLineSegment(sketch, "E279", {"start": v(8.64, -1.37) * mm, "end": v(8.54, -1.92) * mm});
            skSolve(sketch);
        }
        {
            var Q0;
            Q0 = qSketchRegion(id + "F0", true);
            extrude(context, id + "F1", {"entities" : qUnion([Q0]), "depth" : 5 * mm, "offsetDistance" : 25 * mm});
        }
        {
            var Q0;
            Q0=makeQuery(id+"F1.opExtrude","CAP_FACE",FACE,{"disambiguationData":[OSD([sQuery(id+"F0.wireOp",EDGE,"E0"),sQuery(id+"F0.wireOp",EDGE,"E1"),sQuery(id+"F0.wireOp",EDGE,"E2"),sQuery(id+"F0.wireOp",EDGE,"E3"),sQuery(id+"F0.wireOp",EDGE,"E4"),sQuery(id+"F0.wireOp",EDGE,"E5"),sQuery(id+"F0.wireOp",EDGE,"E6"),sQuery(id+"F0.wireOp",EDGE,"E7"),sQuery(id+"F0.wireOp",EDGE,"E8"),sQuery(id+"F0.wireOp",EDGE,"E9"),sQuery(id+"F0.wireOp",EDGE,"E10"),sQuery(id+"F0.wireOp",EDGE,"E11"),sQuery(id+"F0.wireOp",EDGE,"E12"),sQuery(id+"F0.wireOp",EDGE,"E13"),sQuery(id+"F0.wireOp",EDGE,"E14"),sQuery(id+"F0.wireOp",EDGE,"E15"),sQuery(id+"F0.wireOp",EDGE,"E16"),sQuery(id+"F0.wireOp",EDGE,"E17"),sQuery(id+"F0.wireOp",EDGE,"E18"),sQuery(id+"F0.wireOp",EDGE,"E19"),sQuery(id+"F0.wireOp",EDGE,"E20"),sQuery(id+"F0.wireOp",EDGE,"E21"),sQuery(id+"F0.wireOp",EDGE,"E22"),sQuery(id+"F0.wireOp",EDGE,"E23"),sQuery(id+"F0.wireOp",EDGE,"E24"),sQuery(id+"F0.wireOp",EDGE,"E25"),sQuery(id+"F0.wireOp",EDGE,"E26"),sQuery(id+"F0.wireOp",EDGE,"E27"),sQuery(id+"F0.wireOp",EDGE,"E28"),sQuery(id+"F0.wireOp",EDGE,"E29"),sQuery(id+"F0.wireOp",EDGE,"E30"),sQuery(id+"F0.wireOp",EDGE,"E31"),sQuery(id+"F0.wireOp",EDGE,"E32"),sQuery(id+"F0.wireOp",EDGE,"E33"),sQuery(id+"F0.wireOp",EDGE,"E34"),sQuery(id+"F0.wireOp",EDGE,"E35"),sQuery(id+"F0.wireOp",EDGE,"E36"),sQuery(id+"F0.wireOp",EDGE,"E37"),sQuery(id+"F0.wireOp",EDGE,"E38"),sQuery(id+"F0.wireOp",EDGE,"E39"),sQuery(id+"F0.wireOp",EDGE,"E40"),sQuery(id+"F0.wireOp",EDGE,"E41"),sQuery(id+"F0.wireOp",EDGE,"E42"),sQuery(id+"F0.wireOp",EDGE,"E43"),sQuery(id+"F0.wireOp",EDGE,"E44"),sQuery(id+"F0.wireOp",EDGE,"E45"),sQuery(id+"F0.wireOp",EDGE,"E46"),sQuery(id+"F0.wireOp",EDGE,"E47"),sQuery(id+"F0.wireOp",EDGE,"E48"),sQuery(id+"F0.wireOp",EDGE,"E49"),sQuery(id+"F0.wireOp",EDGE,"E50"),sQuery(id+"F0.wireOp",EDGE,"E51"),sQuery(id+"F0.wireOp",EDGE,"E52"),sQuery(id+"F0.wireOp",EDGE,"E53"),sQuery(id+"F0.wireOp",EDGE,"E54"),sQuery(id+"F0.wireOp",EDGE,"E55"),sQuery(id+"F0.wireOp",EDGE,"E56"),sQuery(id+"F0.wireOp",EDGE,"E57"),sQuery(id+"F0.wireOp",EDGE,"E58"),sQuery(id+"F0.wireOp",EDGE,"E59"),sQuery(id+"F0.wireOp",EDGE,"E60"),sQuery(id+"F0.wireOp",EDGE,"E61"),sQuery(id+"F0.wireOp",EDGE,"E62"),sQuery(id+"F0.wireOp",EDGE,"E63"),sQuery(id+"F0.wireOp",EDGE,"E64"),sQuery(id+"F0.wireOp",EDGE,"E65"),sQuery(id+"F0.wireOp",EDGE,"E66"),sQuery(id+"F0.wireOp",EDGE,"E67"),sQuery(id+"F0.wireOp",EDGE,"E68"),sQuery(id+"F0.wireOp",EDGE,"E69"),sQuery(id+"F0.wireOp",EDGE,"E70"),sQuery(id+"F0.wireOp",EDGE,"E71"),sQuery(id+"F0.wireOp",EDGE,"E72"),sQuery(id+"F0.wireOp",EDGE,"E73"),sQuery(id+"F0.wireOp",EDGE,"E74"),sQuery(id+"F0.wireOp",EDGE,"E75"),sQuery(id+"F0.wireOp",EDGE,"E76"),sQuery(id+"F0.wireOp",EDGE,"E77"),sQuery(id+"F0.wireOp",EDGE,"E78"),sQuery(id+"F0.wireOp",EDGE,"E79"),sQuery(id+"F0.wireOp",EDGE,"E80"),sQuery(id+"F0.wireOp",EDGE,"E81"),sQuery(id+"F0.wireOp",EDGE,"E82"),sQuery(id+"F0.wireOp",EDGE,"E83"),sQuery(id+"F0.wireOp",EDGE,"E84"),sQuery(id+"F0.wireOp",EDGE,"E85"),sQuery(id+"F0.wireOp",EDGE,"E86"),sQuery(id+"F0.wireOp",EDGE,"E87"),sQuery(id+"F0.wireOp",EDGE,"E88"),sQuery(id+"F0.wireOp",EDGE,"E89"),sQuery(id+"F0.wireOp",EDGE,"E90"),sQuery(id+"F0.wireOp",EDGE,"E91"),sQuery(id+"F0.wireOp",EDGE,"E92"),sQuery(id+"F0.wireOp",EDGE,"E93"),sQuery(id+"F0.wireOp",EDGE,"E94"),sQuery(id+"F0.wireOp",EDGE,"E95"),sQuery(id+"F0.wireOp",EDGE,"E96"),sQuery(id+"F0.wireOp",EDGE,"E97"),sQuery(id+"F0.wireOp",EDGE,"E98"),sQuery(id+"F0.wireOp",EDGE,"E99"),sQuery(id+"F0.wireOp",EDGE,"E100"),sQuery(id+"F0.wireOp",EDGE,"E101"),sQuery(id+"F0.wireOp",EDGE,"E102"),sQuery(id+"F0.wireOp",EDGE,"E103"),sQuery(id+"F0.wireOp",EDGE,"E104"),sQuery(id+"F0.wireOp",EDGE,"E105"),sQuery(id+"F0.wireOp",EDGE,"E106"),sQuery(id+"F0.wireOp",EDGE,"E107"),sQuery(id+"F0.wireOp",EDGE,"E108"),sQuery(id+"F0.wireOp",EDGE,"E109"),sQuery(id+"F0.wireOp",EDGE,"E110"),sQuery(id+"F0.wireOp",EDGE,"E111"),sQuery(id+"F0.wireOp",EDGE,"E112"),sQuery(id+"F0.wireOp",EDGE,"E113"),sQuery(id+"F0.wireOp",EDGE,"E114"),sQuery(id+"F0.wireOp",EDGE,"E115"),sQuery(id+"F0.wireOp",EDGE,"E116"),sQuery(id+"F0.wireOp",EDGE,"E117"),sQuery(id+"F0.wireOp",EDGE,"E118"),sQuery(id+"F0.wireOp",EDGE,"E119"),sQuery(id+"F0.wireOp",EDGE,"E120"),sQuery(id+"F0.wireOp",EDGE,"E121"),sQuery(id+"F0.wireOp",EDGE,"E122"),sQuery(id+"F0.wireOp",EDGE,"E123"),sQuery(id+"F0.wireOp",EDGE,"E124"),sQuery(id+"F0.wireOp",EDGE,"E125"),sQuery(id+"F0.wireOp",EDGE,"E126"),sQuery(id+"F0.wireOp",EDGE,"E127"),sQuery(id+"F0.wireOp",EDGE,"E128"),sQuery(id+"F0.wireOp",EDGE,"E129"),sQuery(id+"F0.wireOp",EDGE,"E130"),sQuery(id+"F0.wireOp",EDGE,"E131"),sQuery(id+"F0.wireOp",EDGE,"E132"),sQuery(id+"F0.wireOp",EDGE,"E133"),sQuery(id+"F0.wireOp",EDGE,"E134"),sQuery(id+"F0.wireOp",EDGE,"E135"),sQuery(id+"F0.wireOp",EDGE,"E136"),sQuery(id+"F0.wireOp",EDGE,"E137"),sQuery(id+"F0.wireOp",EDGE,"E138"),sQuery(id+"F0.wireOp",EDGE,"E139"),sQuery(id+"F0.wireOp",EDGE,"E140"),sQuery(id+"F0.wireOp",EDGE,"E141"),sQuery(id+"F0.wireOp",EDGE,"E142"),sQuery(id+"F0.wireOp",EDGE,"E143"),sQuery(id+"F0.wireOp",EDGE,"E144"),sQuery(id+"F0.wireOp",EDGE,"E145"),sQuery(id+"F0.wireOp",EDGE,"E146"),sQuery(id+"F0.wireOp",EDGE,"E147"),sQuery(id+"F0.wireOp",EDGE,"E148"),sQuery(id+"F0.wireOp",EDGE,"E149"),sQuery(id+"F0.wireOp",EDGE,"E150"),sQuery(id+"F0.wireOp",EDGE,"E151"),sQuery(id+"F0.wireOp",EDGE,"E152"),sQuery(id+"F0.wireOp",EDGE,"E153"),sQuery(id+"F0.wireOp",EDGE,"E154"),sQuery(id+"F0.wireOp",EDGE,"E155"),sQuery(id+"F0.wireOp",EDGE,"E156"),sQuery(id+"F0.wireOp",EDGE,"E157"),sQuery(id+"F0.wireOp",EDGE,"E158"),sQuery(id+"F0.wireOp",EDGE,"E159"),sQuery(id+"F0.wireOp",EDGE,"E160"),sQuery(id+"F0.wireOp",EDGE,"E161"),sQuery(id+"F0.wireOp",EDGE,"E162"),sQuery(id+"F0.wireOp",EDGE,"E163"),sQuery(id+"F0.wireOp",EDGE,"E164"),sQuery(id+"F0.wireOp",EDGE,"E165"),sQuery(id+"F0.wireOp",EDGE,"E166"),sQuery(id+"F0.wireOp",EDGE,"E167"),sQuery(id+"F0.wireOp",EDGE,"E168"),sQuery(id+"F0.wireOp",EDGE,"E169"),sQuery(id+"F0.wireOp",EDGE,"E170"),sQuery(id+"F0.wireOp",EDGE,"E171"),sQuery(id+"F0.wireOp",EDGE,"E172"),sQuery(id+"F0.wireOp",EDGE,"E173"),sQuery(id+"F0.wireOp",EDGE,"E174"),sQuery(id+"F0.wireOp",EDGE,"E175"),sQuery(id+"F0.wireOp",EDGE,"E176"),sQuery(id+"F0.wireOp",EDGE,"E177"),sQuery(id+"F0.wireOp",EDGE,"E178"),sQuery(id+"F0.wireOp",EDGE,"E179"),sQuery(id+"F0.wireOp",EDGE,"E180"),sQuery(id+"F0.wireOp",EDGE,"E181"),sQuery(id+"F0.wireOp",EDGE,"E182"),sQuery(id+"F0.wireOp",EDGE,"E183"),sQuery(id+"F0.wireOp",EDGE,"E184"),sQuery(id+"F0.wireOp",EDGE,"E185"),sQuery(id+"F0.wireOp",EDGE,"E186"),sQuery(id+"F0.wireOp",EDGE,"E187"),sQuery(id+"F0.wireOp",EDGE,"E188"),sQuery(id+"F0.wireOp",EDGE,"E189"),sQuery(id+"F0.wireOp",EDGE,"E190"),sQuery(id+"F0.wireOp",EDGE,"E191"),sQuery(id+"F0.wireOp",EDGE,"E192"),sQuery(id+"F0.wireOp",EDGE,"E193"),sQuery(id+"F0.wireOp",EDGE,"E194"),sQuery(id+"F0.wireOp",EDGE,"E195"),sQuery(id+"F0.wireOp",EDGE,"E196"),sQuery(id+"F0.wireOp",EDGE,"E197"),sQuery(id+"F0.wireOp",EDGE,"E198"),sQuery(id+"F0.wireOp",EDGE,"E199"),sQuery(id+"F0.wireOp",EDGE,"E200"),sQuery(id+"F0.wireOp",EDGE,"E201"),sQuery(id+"F0.wireOp",EDGE,"E202"),sQuery(id+"F0.wireOp",EDGE,"E203"),sQuery(id+"F0.wireOp",EDGE,"E204"),sQuery(id+"F0.wireOp",EDGE,"E205"),sQuery(id+"F0.wireOp",EDGE,"E206"),sQuery(id+"F0.wireOp",EDGE,"E207"),sQuery(id+"F0.wireOp",EDGE,"E208"),sQuery(id+"F0.wireOp",EDGE,"E209"),sQuery(id+"F0.wireOp",EDGE,"E210"),sQuery(id+"F0.wireOp",EDGE,"E211"),sQuery(id+"F0.wireOp",EDGE,"E212"),sQuery(id+"F0.wireOp",EDGE,"E213"),sQuery(id+"F0.wireOp",EDGE,"E214"),sQuery(id+"F0.wireOp",EDGE,"E215"),sQuery(id+"F0.wireOp",EDGE,"E216"),sQuery(id+"F0.wireOp",EDGE,"E217"),sQuery(id+"F0.wireOp",EDGE,"E218"),sQuery(id+"F0.wireOp",EDGE,"E219"),sQuery(id+"F0.wireOp",EDGE,"E220"),sQuery(id+"F0.wireOp",EDGE,"E221"),sQuery(id+"F0.wireOp",EDGE,"E222"),sQuery(id+"F0.wireOp",EDGE,"E223"),sQuery(id+"F0.wireOp",EDGE,"E224"),sQuery(id+"F0.wireOp",EDGE,"E225"),sQuery(id+"F0.wireOp",EDGE,"E226"),sQuery(id+"F0.wireOp",EDGE,"E227"),sQuery(id+"F0.wireOp",EDGE,"E228"),sQuery(id+"F0.wireOp",EDGE,"E229"),sQuery(id+"F0.wireOp",EDGE,"E230"),sQuery(id+"F0.wireOp",EDGE,"E231"),sQuery(id+"F0.wireOp",EDGE,"E232"),sQuery(id+"F0.wireOp",EDGE,"E233"),sQuery(id+"F0.wireOp",EDGE,"E234"),sQuery(id+"F0.wireOp",EDGE,"E235"),sQuery(id+"F0.wireOp",EDGE,"E236"),sQuery(id+"F0.wireOp",EDGE,"E237"),sQuery(id+"F0.wireOp",EDGE,"E238"),sQuery(id+"F0.wireOp",EDGE,"E239"),sQuery(id+"F0.wireOp",EDGE,"E240"),sQuery(id+"F0.wireOp",EDGE,"E241"),sQuery(id+"F0.wireOp",EDGE,"E242"),sQuery(id+"F0.wireOp",EDGE,"E243"),sQuery(id+"F0.wireOp",EDGE,"E244"),sQuery(id+"F0.wireOp",EDGE,"E245"),sQuery(id+"F0.wireOp",EDGE,"E246"),sQuery(id+"F0.wireOp",EDGE,"E247"),sQuery(id+"F0.wireOp",EDGE,"E248"),sQuery(id+"F0.wireOp",EDGE,"E249"),sQuery(id+"F0.wireOp",EDGE,"E250"),sQuery(id+"F0.wireOp",EDGE,"E251"),sQuery(id+"F0.wireOp",EDGE,"E252"),sQuery(id+"F0.wireOp",EDGE,"E253"),sQuery(id+"F0.wireOp",EDGE,"E254"),sQuery(id+"F0.wireOp",EDGE,"E255"),sQuery(id+"F0.wireOp",EDGE,"E256"),sQuery(id+"F0.wireOp",EDGE,"E257"),sQuery(id+"F0.wireOp",EDGE,"E258"),sQuery(id+"F0.wireOp",EDGE,"E259"),sQuery(id+"F0.wireOp",EDGE,"E260"),sQuery(id+"F0.wireOp",EDGE,"E261"),sQuery(id+"F0.wireOp",EDGE,"E262"),sQuery(id+"F0.wireOp",EDGE,"E263"),sQuery(id+"F0.wireOp",EDGE,"E264"),sQuery(id+"F0.wireOp",EDGE,"E265"),sQuery(id+"F0.wireOp",EDGE,"E266"),sQuery(id+"F0.wireOp",EDGE,"E267"),sQuery(id+"F0.wireOp",EDGE,"E268"),sQuery(id+"F0.wireOp",EDGE,"E269"),sQuery(id+"F0.wireOp",EDGE,"E270"),sQuery(id+"F0.wireOp",EDGE,"E271"),sQuery(id+"F0.wireOp",EDGE,"E272"),sQuery(id+"F0.wireOp",EDGE,"E273"),sQuery(id+"F0.wireOp",EDGE,"E274"),sQuery(id+"F0.wireOp",EDGE,"E275"),sQuery(id+"F0.wireOp",EDGE,"E276"),sQuery(id+"F0.wireOp",EDGE,"E277"),sQuery(id+"F0.wireOp",EDGE,"E278"),sQuery(id+"F0.wireOp",EDGE,"E279")])],"isStart":false});
            var sketch = newSketch(context, id + "F2", { "sketchPlane" : qUnion([Q0])});
            skCircle(sketch, "E280", {"center": v(0, 0) * mm, "radius": 4.5 * mm});
            skCircle(sketch, "E281", {"center": v(0, 6) * mm, "radius": 1 * mm});
            skCircle(sketch, "E282.1.0", {"center": v(-4.24, 4.24) * mm, "radius": 1 * mm});
            skCircle(sketch, "E282.2.0", {"center": v(-6, 0) * mm, "radius": 1 * mm});
            skCircle(sketch, "E283.1.3.0", {"center": v(-4.24, -4.24) * mm, "radius": 1 * mm});
            skCircle(sketch, "E283.1.4.0", {"center": v(0, -6) * mm, "radius": 1 * mm});
            skCircle(sketch, "E283.1.5.0", {"center": v(4.24, -4.24) * mm, "radius": 1 * mm});
            skCircle(sketch, "E283.1.6.0", {"center": v(6, 0) * mm, "radius": 1 * mm});
            skCircle(sketch, "E283.1.7.0", {"center": v(4.24, 4.24) * mm, "radius": 1 * mm});
            skLineSegment(sketch, "E284", {"start": v(0, 11) * mm, "end": v(0, -11) * mm, "construction": true});
            skSolve(sketch);
        }
        {
            var Q0;
            Q0 = qSketchRegion(id + "F2", true);
            extrude(context, id + "F3", {"entities" : qUnion([Q0]), "operationType" : NewBodyOperationType.REMOVE, "endBound" : BoundingType.UP_TO_NEXT, "oppositeDirection" : true, "depth" : 25 * mm, "offsetDistance" : 25 * mm});
        }
        {
            var Q0;
            Q0=qCreatedBy(makeId("Front.planeOp"),FACE);
            var sketch = newSketch(context, id + "F4", { "sketchPlane" : qUnion([Q0])});
            skLineSegment(sketch, "E285", {"start": v(13.75, 0) * mm, "end": v(13.74, 0.51) * mm});
            skLineSegment(sketch, "E286", {"start": v(13.74, 0.51) * mm, "end": v(14.19, 0.54) * mm});
            skLineSegment(sketch, "E287", {"start": v(14.19, 0.54) * mm, "end": v(14.64, 0.65) * mm});
            skLineSegment(sketch, "E288", {"start": v(14.64, 0.65) * mm, "end": v(15.08, 0.83) * mm});
            skLineSegment(sketch, "E289", {"start": v(15.08, 0.83) * mm, "end": v(15.51, 1.05) * mm});
            skLineSegment(sketch, "E290", {"start": v(15.51, 1.05) * mm, "end": v(15.95, 1.3) * mm});
            skLineSegment(sketch, "E291", {"start": v(15.95, 1.3) * mm, "end": v(15.91, 1.67) * mm});
            skLineSegment(sketch, "E292", {"start": v(15.91, 1.67) * mm, "end": v(15.87, 2.04) * mm});
            skLineSegment(sketch, "E293", {"start": v(15.87, 2.04) * mm, "end": v(15.4, 2.2) * mm});
            skLineSegment(sketch, "E294", {"start": v(15.4, 2.2) * mm, "end": v(14.92, 2.33) * mm});
            skLineSegment(sketch, "E295", {"start": v(14.92, 2.33) * mm, "end": v(14.45, 2.4) * mm});
            skLineSegment(sketch, "E296", {"start": v(14.45, 2.4) * mm, "end": v(14, 2.42) * mm});
            skLineSegment(sketch, "E297", {"start": v(14, 2.42) * mm, "end": v(13.55, 2.35) * mm});
            skLineSegment(sketch, "E298", {"start": v(13.55, 2.35) * mm, "end": v(13.45, 2.86) * mm});
            skLineSegment(sketch, "E299", {"start": v(13.45, 2.86) * mm, "end": v(13.33, 3.36) * mm});
            skLineSegment(sketch, "E300", {"start": v(13.33, 3.36) * mm, "end": v(13.77, 3.48) * mm});
            skLineSegment(sketch, "E301", {"start": v(13.77, 3.48) * mm, "end": v(14.18, 3.68) * mm});
            skLineSegment(sketch, "E302", {"start": v(14.18, 3.68) * mm, "end": v(14.58, 3.94) * mm});
            skLineSegment(sketch, "E303", {"start": v(14.58, 3.94) * mm, "end": v(14.96, 4.25) * mm});
            skLineSegment(sketch, "E304", {"start": v(14.96, 4.25) * mm, "end": v(15.33, 4.6) * mm});
            skLineSegment(sketch, "E305", {"start": v(15.33, 4.6) * mm, "end": v(15.22, 4.94) * mm});
            skLineSegment(sketch, "E306", {"start": v(15.22, 4.94) * mm, "end": v(15.1, 5.3) * mm});
            skLineSegment(sketch, "E307", {"start": v(15.1, 5.3) * mm, "end": v(14.6, 5.35) * mm});
            skLineSegment(sketch, "E308", {"start": v(14.6, 5.35) * mm, "end": v(14.11, 5.38) * mm});
            skLineSegment(sketch, "E309", {"start": v(14.11, 5.38) * mm, "end": v(13.64, 5.35) * mm});
            skLineSegment(sketch, "E310", {"start": v(13.64, 5.35) * mm, "end": v(13.18, 5.28) * mm});
            skLineSegment(sketch, "E311", {"start": v(13.18, 5.28) * mm, "end": v(12.76, 5.12) * mm});
            skLineSegment(sketch, "E312", {"start": v(12.76, 5.12) * mm, "end": v(12.56, 5.6) * mm});
            skLineSegment(sketch, "E313", {"start": v(12.56, 5.6) * mm, "end": v(12.34, 6.06) * mm});
            skLineSegment(sketch, "E314", {"start": v(12.34, 6.06) * mm, "end": v(12.74, 6.27) * mm});
            skLineSegment(sketch, "E315", {"start": v(12.74, 6.27) * mm, "end": v(13.1, 6.55) * mm});
            skLineSegment(sketch, "E316", {"start": v(13.1, 6.55) * mm, "end": v(13.44, 6.89) * mm});
            skLineSegment(sketch, "E317", {"start": v(13.44, 6.89) * mm, "end": v(13.75, 7.27) * mm});
            skLineSegment(sketch, "E318", {"start": v(13.75, 7.27) * mm, "end": v(14.04, 7.68) * mm});
            skLineSegment(sketch, "E319", {"start": v(14.04, 7.68) * mm, "end": v(13.86, 8) * mm});
            skLineSegment(sketch, "E320", {"start": v(13.86, 8) * mm, "end": v(13.67, 8.32) * mm});
            skLineSegment(sketch, "E321", {"start": v(13.67, 8.32) * mm, "end": v(13.17, 8.27) * mm});
            skLineSegment(sketch, "E322", {"start": v(13.17, 8.27) * mm, "end": v(12.68, 8.2) * mm});
            skLineSegment(sketch, "E323", {"start": v(12.68, 8.2) * mm, "end": v(12.22, 8.07) * mm});
            skLineSegment(sketch, "E324", {"start": v(12.22, 8.07) * mm, "end": v(11.8, 7.9) * mm});
            skLineSegment(sketch, "E325", {"start": v(11.8, 7.9) * mm, "end": v(11.42, 7.66) * mm});
            skLineSegment(sketch, "E326", {"start": v(11.42, 7.66) * mm, "end": v(11.12, 8.08) * mm});
            skLineSegment(sketch, "E327", {"start": v(11.12, 8.08) * mm, "end": v(10.81, 8.5) * mm});
            skLineSegment(sketch, "E328", {"start": v(10.81, 8.5) * mm, "end": v(11.16, 8.78) * mm});
            skLineSegment(sketch, "E329", {"start": v(11.16, 8.78) * mm, "end": v(11.46, 9.13) * mm});
            skLineSegment(sketch, "E330", {"start": v(11.46, 9.13) * mm, "end": v(11.71, 9.53) * mm});
            skLineSegment(sketch, "E331", {"start": v(11.71, 9.53) * mm, "end": v(11.94, 9.97) * mm});
            skLineSegment(sketch, "E332", {"start": v(11.94, 9.97) * mm, "end": v(12.13, 10.43) * mm});
            skLineSegment(sketch, "E333", {"start": v(12.13, 10.43) * mm, "end": v(11.9, 10.7) * mm});
            skLineSegment(sketch, "E334", {"start": v(11.9, 10.7) * mm, "end": v(11.64, 10.98) * mm});
            skLineSegment(sketch, "E335", {"start": v(11.64, 10.98) * mm, "end": v(11.16, 10.83) * mm});
            skLineSegment(sketch, "E336", {"start": v(11.16, 10.83) * mm, "end": v(10.7, 10.65) * mm});
            skLineSegment(sketch, "E337", {"start": v(10.7, 10.65) * mm, "end": v(10.28, 10.44) * mm});
            skLineSegment(sketch, "E338", {"start": v(10.28, 10.44) * mm, "end": v(9.9, 10.18) * mm});
            skLineSegment(sketch, "E339", {"start": v(9.9, 10.18) * mm, "end": v(9.58, 9.87) * mm});
            skLineSegment(sketch, "E340", {"start": v(9.58, 9.87) * mm, "end": v(9.2, 10.22) * mm});
            skLineSegment(sketch, "E341", {"start": v(9.2, 10.22) * mm, "end": v(8.81, 10.56) * mm});
            skLineSegment(sketch, "E342", {"start": v(8.81, 10.56) * mm, "end": v(9.1, 10.9) * mm});
            skLineSegment(sketch, "E343", {"start": v(9.1, 10.9) * mm, "end": v(9.3, 11.31) * mm});
            skLineSegment(sketch, "E344", {"start": v(9.3, 11.31) * mm, "end": v(9.47, 11.76) * mm});
            skLineSegment(sketch, "E345", {"start": v(9.47, 11.76) * mm, "end": v(9.6, 12.23) * mm});
            skLineSegment(sketch, "E346", {"start": v(9.6, 12.23) * mm, "end": v(9.7, 12.72) * mm});
            skLineSegment(sketch, "E347", {"start": v(9.7, 12.72) * mm, "end": v(9.4, 12.94) * mm});
            skLineSegment(sketch, "E348", {"start": v(9.4, 12.94) * mm, "end": v(9.1, 13.16) * mm});
            skLineSegment(sketch, "E349", {"start": v(9.1, 13.16) * mm, "end": v(8.66, 12.91) * mm});
            skLineSegment(sketch, "E350", {"start": v(8.66, 12.91) * mm, "end": v(8.26, 12.64) * mm});
            skLineSegment(sketch, "E351", {"start": v(8.26, 12.64) * mm, "end": v(7.88, 12.35) * mm});
            skLineSegment(sketch, "E352", {"start": v(7.88, 12.35) * mm, "end": v(7.56, 12.02) * mm});
            skLineSegment(sketch, "E353", {"start": v(7.56, 12.02) * mm, "end": v(7.32, 11.64) * mm});
            skLineSegment(sketch, "E354", {"start": v(7.32, 11.64) * mm, "end": v(6.88, 11.9) * mm});
            skLineSegment(sketch, "E355", {"start": v(6.88, 11.9) * mm, "end": v(6.42, 12.16) * mm});
            skLineSegment(sketch, "E356", {"start": v(6.42, 12.16) * mm, "end": v(6.63, 12.56) * mm});
            skLineSegment(sketch, "E357", {"start": v(6.63, 12.56) * mm, "end": v(6.75, 13) * mm});
            skLineSegment(sketch, "E358", {"start": v(6.75, 13) * mm, "end": v(6.82, 13.47) * mm});
            skLineSegment(sketch, "E359", {"start": v(6.82, 13.47) * mm, "end": v(6.85, 13.96) * mm});
            skLineSegment(sketch, "E360", {"start": v(6.85, 13.96) * mm, "end": v(6.84, 14.46) * mm});
            skLineSegment(sketch, "E361", {"start": v(6.84, 14.46) * mm, "end": v(6.5, 14.62) * mm});
            skLineSegment(sketch, "E362", {"start": v(6.5, 14.62) * mm, "end": v(6.17, 14.76) * mm});
            skLineSegment(sketch, "E363", {"start": v(6.17, 14.76) * mm, "end": v(5.79, 14.43) * mm});
            skLineSegment(sketch, "E364", {"start": v(5.79, 14.43) * mm, "end": v(5.45, 14.08) * mm});
            skLineSegment(sketch, "E365", {"start": v(5.45, 14.08) * mm, "end": v(5.14, 13.72) * mm});
            skLineSegment(sketch, "E366", {"start": v(5.14, 13.72) * mm, "end": v(4.9, 13.33) * mm});
            skLineSegment(sketch, "E367", {"start": v(4.9, 13.33) * mm, "end": v(4.74, 12.9) * mm});
            skLineSegment(sketch, "E368", {"start": v(4.74, 12.9) * mm, "end": v(4.25, 13.08) * mm});
            skLineSegment(sketch, "E369", {"start": v(4.25, 13.08) * mm, "end": v(3.76, 13.23) * mm});
            skLineSegment(sketch, "E370", {"start": v(3.76, 13.23) * mm, "end": v(3.87, 13.66) * mm});
            skLineSegment(sketch, "E371", {"start": v(3.87, 13.66) * mm, "end": v(3.9, 14.12) * mm});
            skLineSegment(sketch, "E372", {"start": v(3.9, 14.12) * mm, "end": v(3.87, 14.6) * mm});
            skLineSegment(sketch, "E373", {"start": v(3.87, 14.6) * mm, "end": v(3.8, 15.08) * mm});
            skLineSegment(sketch, "E374", {"start": v(3.8, 15.08) * mm, "end": v(3.69, 15.57) * mm});
            skLineSegment(sketch, "E375", {"start": v(3.69, 15.57) * mm, "end": v(3.33, 15.65) * mm});
            skLineSegment(sketch, "E376", {"start": v(3.33, 15.65) * mm, "end": v(2.97, 15.72) * mm});
            skLineSegment(sketch, "E377", {"start": v(2.97, 15.72) * mm, "end": v(2.66, 15.32) * mm});
            skLineSegment(sketch, "E378", {"start": v(2.66, 15.32) * mm, "end": v(2.4, 14.9) * mm});
            skLineSegment(sketch, "E379", {"start": v(2.4, 14.9) * mm, "end": v(2.18, 14.49) * mm});
            skLineSegment(sketch, "E380", {"start": v(2.18, 14.49) * mm, "end": v(2.02, 14.06) * mm});
            skLineSegment(sketch, "E381", {"start": v(2.02, 14.06) * mm, "end": v(1.95, 13.61) * mm});
            skLineSegment(sketch, "E382", {"start": v(1.95, 13.61) * mm, "end": v(1.44, 13.67) * mm});
            skLineSegment(sketch, "E383", {"start": v(1.44, 13.67) * mm, "end": v(0.92, 13.72) * mm});
            skLineSegment(sketch, "E384", {"start": v(0.92, 13.72) * mm, "end": v(0.95, 14.17) * mm});
            skLineSegment(sketch, "E385", {"start": v(0.95, 14.17) * mm, "end": v(0.88, 14.62) * mm});
            skLineSegment(sketch, "E386", {"start": v(0.88, 14.62) * mm, "end": v(0.75, 15.08) * mm});
            skLineSegment(sketch, "E387", {"start": v(0.75, 15.08) * mm, "end": v(0.58, 15.54) * mm});
            skLineSegment(sketch, "E388", {"start": v(0.58, 15.54) * mm, "end": v(0.37, 16) * mm});
            skLineSegment(sketch, "E389", {"start": v(0.37, 16) * mm, "end": v(0, 16) * mm});
            skLineSegment(sketch, "E390", {"start": v(0, 16) * mm, "end": v(-0.37, 16) * mm});
            skLineSegment(sketch, "E391", {"start": v(-0.37, 16) * mm, "end": v(-0.58, 15.54) * mm});
            skLineSegment(sketch, "E392", {"start": v(-0.58, 15.54) * mm, "end": v(-0.75, 15.08) * mm});
            skLineSegment(sketch, "E393", {"start": v(-0.75, 15.08) * mm, "end": v(-0.88, 14.62) * mm});
            skLineSegment(sketch, "E394", {"start": v(-0.88, 14.62) * mm, "end": v(-0.95, 14.17) * mm});
            skLineSegment(sketch, "E395", {"start": v(-0.95, 14.17) * mm, "end": v(-0.92, 13.72) * mm});
            skLineSegment(sketch, "E396", {"start": v(-0.92, 13.72) * mm, "end": v(-1.44, 13.67) * mm});
            skLineSegment(sketch, "E397", {"start": v(-1.44, 13.67) * mm, "end": v(-1.95, 13.61) * mm});
            skLineSegment(sketch, "E398", {"start": v(-1.95, 13.61) * mm, "end": v(-2.02, 14.06) * mm});
            skLineSegment(sketch, "E399", {"start": v(-2.02, 14.06) * mm, "end": v(-2.18, 14.49) * mm});
            skLineSegment(sketch, "E400", {"start": v(-2.18, 14.49) * mm, "end": v(-2.4, 14.9) * mm});
            skLineSegment(sketch, "E401", {"start": v(-2.4, 14.9) * mm, "end": v(-2.66, 15.32) * mm});
            skLineSegment(sketch, "E402", {"start": v(-2.66, 15.32) * mm, "end": v(-2.97, 15.72) * mm});
            skLineSegment(sketch, "E403", {"start": v(-2.97, 15.72) * mm, "end": v(-3.33, 15.65) * mm});
            skLineSegment(sketch, "E404", {"start": v(-3.33, 15.65) * mm, "end": v(-3.69, 15.57) * mm});
            skLineSegment(sketch, "E405", {"start": v(-3.69, 15.57) * mm, "end": v(-3.8, 15.08) * mm});
            skLineSegment(sketch, "E406", {"start": v(-3.8, 15.08) * mm, "end": v(-3.87, 14.6) * mm});
            skLineSegment(sketch, "E407", {"start": v(-3.87, 14.6) * mm, "end": v(-3.9, 14.12) * mm});
            skLineSegment(sketch, "E408", {"start": v(-3.9, 14.12) * mm, "end": v(-3.87, 13.66) * mm});
            skLineSegment(sketch, "E409", {"start": v(-3.87, 13.66) * mm, "end": v(-3.76, 13.23) * mm});
            skLineSegment(sketch, "E410", {"start": v(-3.76, 13.23) * mm, "end": v(-4.25, 13.08) * mm});
            skLineSegment(sketch, "E411", {"start": v(-4.25, 13.08) * mm, "end": v(-4.74, 12.9) * mm});
            skLineSegment(sketch, "E412", {"start": v(-4.74, 12.9) * mm, "end": v(-4.9, 13.33) * mm});
            skLineSegment(sketch, "E413", {"start": v(-4.9, 13.33) * mm, "end": v(-5.14, 13.72) * mm});
            skLineSegment(sketch, "E414", {"start": v(-5.14, 13.72) * mm, "end": v(-5.45, 14.08) * mm});
            skLineSegment(sketch, "E415", {"start": v(-5.45, 14.08) * mm, "end": v(-5.79, 14.43) * mm});
            skLineSegment(sketch, "E416", {"start": v(-5.79, 14.43) * mm, "end": v(-6.17, 14.76) * mm});
            skLineSegment(sketch, "E417", {"start": v(-6.17, 14.76) * mm, "end": v(-6.5, 14.62) * mm});
            skLineSegment(sketch, "E418", {"start": v(-6.5, 14.62) * mm, "end": v(-6.84, 14.46) * mm});
            skLineSegment(sketch, "E419", {"start": v(-6.84, 14.46) * mm, "end": v(-6.85, 13.96) * mm});
            skLineSegment(sketch, "E420", {"start": v(-6.85, 13.96) * mm, "end": v(-6.82, 13.47) * mm});
            skLineSegment(sketch, "E421", {"start": v(-6.82, 13.47) * mm, "end": v(-6.75, 13) * mm});
            skLineSegment(sketch, "E422", {"start": v(-6.75, 13) * mm, "end": v(-6.63, 12.56) * mm});
            skLineSegment(sketch, "E423", {"start": v(-6.63, 12.56) * mm, "end": v(-6.42, 12.16) * mm});
            skLineSegment(sketch, "E424", {"start": v(-6.42, 12.16) * mm, "end": v(-6.88, 11.9) * mm});
            skLineSegment(sketch, "E425", {"start": v(-6.88, 11.9) * mm, "end": v(-7.32, 11.64) * mm});
            skLineSegment(sketch, "E426", {"start": v(-7.32, 11.64) * mm, "end": v(-7.56, 12.02) * mm});
            skLineSegment(sketch, "E427", {"start": v(-7.56, 12.02) * mm, "end": v(-7.88, 12.35) * mm});
            skLineSegment(sketch, "E428", {"start": v(-7.88, 12.35) * mm, "end": v(-8.26, 12.64) * mm});
            skLineSegment(sketch, "E429", {"start": v(-8.26, 12.64) * mm, "end": v(-8.66, 12.91) * mm});
            skLineSegment(sketch, "E430", {"start": v(-8.66, 12.91) * mm, "end": v(-9.1, 13.16) * mm});
            skLineSegment(sketch, "E431", {"start": v(-9.1, 13.16) * mm, "end": v(-9.4, 12.94) * mm});
            skLineSegment(sketch, "E432", {"start": v(-9.4, 12.94) * mm, "end": v(-9.7, 12.72) * mm});
            skLineSegment(sketch, "E433", {"start": v(-9.7, 12.72) * mm, "end": v(-9.6, 12.23) * mm});
            skLineSegment(sketch, "E434", {"start": v(-9.6, 12.23) * mm, "end": v(-9.47, 11.76) * mm});
            skLineSegment(sketch, "E435", {"start": v(-9.47, 11.76) * mm, "end": v(-9.3, 11.31) * mm});
            skLineSegment(sketch, "E436", {"start": v(-9.3, 11.31) * mm, "end": v(-9.1, 10.9) * mm});
            skLineSegment(sketch, "E437", {"start": v(-9.1, 10.9) * mm, "end": v(-8.81, 10.56) * mm});
            skLineSegment(sketch, "E438", {"start": v(-8.81, 10.56) * mm, "end": v(-9.2, 10.22) * mm});
            skLineSegment(sketch, "E439", {"start": v(-9.2, 10.22) * mm, "end": v(-9.58, 9.87) * mm});
            skLineSegment(sketch, "E440", {"start": v(-9.58, 9.87) * mm, "end": v(-9.9, 10.18) * mm});
            skLineSegment(sketch, "E441", {"start": v(-9.9, 10.18) * mm, "end": v(-10.28, 10.44) * mm});
            skLineSegment(sketch, "E442", {"start": v(-10.28, 10.44) * mm, "end": v(-10.7, 10.65) * mm});
            skLineSegment(sketch, "E443", {"start": v(-10.7, 10.65) * mm, "end": v(-11.16, 10.83) * mm});
            skLineSegment(sketch, "E444", {"start": v(-11.16, 10.83) * mm, "end": v(-11.64, 10.98) * mm});
            skLineSegment(sketch, "E445", {"start": v(-11.64, 10.98) * mm, "end": v(-11.9, 10.7) * mm});
            skLineSegment(sketch, "E446", {"start": v(-11.9, 10.7) * mm, "end": v(-12.13, 10.43) * mm});
            skLineSegment(sketch, "E447", {"start": v(-12.13, 10.43) * mm, "end": v(-11.94, 9.97) * mm});
            skLineSegment(sketch, "E448", {"start": v(-11.94, 9.97) * mm, "end": v(-11.71, 9.53) * mm});
            skLineSegment(sketch, "E449", {"start": v(-11.71, 9.53) * mm, "end": v(-11.46, 9.13) * mm});
            skLineSegment(sketch, "E450", {"start": v(-11.46, 9.13) * mm, "end": v(-11.16, 8.78) * mm});
            skLineSegment(sketch, "E451", {"start": v(-11.16, 8.78) * mm, "end": v(-10.81, 8.5) * mm});
            skLineSegment(sketch, "E452", {"start": v(-10.81, 8.5) * mm, "end": v(-11.12, 8.08) * mm});
            skLineSegment(sketch, "E453", {"start": v(-11.12, 8.08) * mm, "end": v(-11.42, 7.66) * mm});
            skLineSegment(sketch, "E454", {"start": v(-11.42, 7.66) * mm, "end": v(-11.8, 7.9) * mm});
            skLineSegment(sketch, "E455", {"start": v(-11.8, 7.9) * mm, "end": v(-12.22, 8.07) * mm});
            skLineSegment(sketch, "E456", {"start": v(-12.22, 8.07) * mm, "end": v(-12.68, 8.2) * mm});
            skLineSegment(sketch, "E457", {"start": v(-12.68, 8.2) * mm, "end": v(-13.17, 8.27) * mm});
            skLineSegment(sketch, "E458", {"start": v(-13.17, 8.27) * mm, "end": v(-13.67, 8.32) * mm});
            skLineSegment(sketch, "E459", {"start": v(-13.67, 8.32) * mm, "end": v(-13.86, 8) * mm});
            skLineSegment(sketch, "E460", {"start": v(-13.86, 8) * mm, "end": v(-14.04, 7.68) * mm});
            skLineSegment(sketch, "E461", {"start": v(-14.04, 7.68) * mm, "end": v(-13.75, 7.27) * mm});
            skLineSegment(sketch, "E462", {"start": v(-13.75, 7.27) * mm, "end": v(-13.44, 6.89) * mm});
            skLineSegment(sketch, "E463", {"start": v(-13.44, 6.89) * mm, "end": v(-13.1, 6.55) * mm});
            skLineSegment(sketch, "E464", {"start": v(-13.1, 6.55) * mm, "end": v(-12.74, 6.27) * mm});
            skLineSegment(sketch, "E465", {"start": v(-12.74, 6.27) * mm, "end": v(-12.34, 6.06) * mm});
            skLineSegment(sketch, "E466", {"start": v(-12.34, 6.06) * mm, "end": v(-12.56, 5.6) * mm});
            skLineSegment(sketch, "E467", {"start": v(-12.56, 5.6) * mm, "end": v(-12.76, 5.12) * mm});
            skLineSegment(sketch, "E468", {"start": v(-12.76, 5.12) * mm, "end": v(-13.18, 5.28) * mm});
            skLineSegment(sketch, "E469", {"start": v(-13.18, 5.28) * mm, "end": v(-13.64, 5.35) * mm});
            skLineSegment(sketch, "E470", {"start": v(-13.64, 5.35) * mm, "end": v(-14.11, 5.38) * mm});
            skLineSegment(sketch, "E471", {"start": v(-14.11, 5.38) * mm, "end": v(-14.6, 5.35) * mm});
            skLineSegment(sketch, "E472", {"start": v(-14.6, 5.35) * mm, "end": v(-15.1, 5.3) * mm});
            skLineSegment(sketch, "E473", {"start": v(-15.1, 5.3) * mm, "end": v(-15.22, 4.94) * mm});
            skLineSegment(sketch, "E474", {"start": v(-15.22, 4.94) * mm, "end": v(-15.33, 4.6) * mm});
            skLineSegment(sketch, "E475", {"start": v(-15.33, 4.6) * mm, "end": v(-14.96, 4.25) * mm});
            skLineSegment(sketch, "E476", {"start": v(-14.96, 4.25) * mm, "end": v(-14.58, 3.94) * mm});
            skLineSegment(sketch, "E477", {"start": v(-14.58, 3.94) * mm, "end": v(-14.18, 3.68) * mm});
            skLineSegment(sketch, "E478", {"start": v(-14.18, 3.68) * mm, "end": v(-13.77, 3.48) * mm});
            skLineSegment(sketch, "E479", {"start": v(-13.77, 3.48) * mm, "end": v(-13.33, 3.36) * mm});
            skLineSegment(sketch, "E480", {"start": v(-13.33, 3.36) * mm, "end": v(-13.45, 2.86) * mm});
            skLineSegment(sketch, "E481", {"start": v(-13.45, 2.86) * mm, "end": v(-13.55, 2.35) * mm});
            skLineSegment(sketch, "E482", {"start": v(-13.55, 2.35) * mm, "end": v(-14, 2.42) * mm});
            skLineSegment(sketch, "E483", {"start": v(-14, 2.42) * mm, "end": v(-14.45, 2.4) * mm});
            skLineSegment(sketch, "E484", {"start": v(-14.45, 2.4) * mm, "end": v(-14.92, 2.33) * mm});
            skLineSegment(sketch, "E485", {"start": v(-14.92, 2.33) * mm, "end": v(-15.4, 2.2) * mm});
            skLineSegment(sketch, "E486", {"start": v(-15.4, 2.2) * mm, "end": v(-15.87, 2.04) * mm});
            skLineSegment(sketch, "E487", {"start": v(-15.87, 2.04) * mm, "end": v(-15.91, 1.67) * mm});
            skLineSegment(sketch, "E488", {"start": v(-15.91, 1.67) * mm, "end": v(-15.95, 1.3) * mm});
            skLineSegment(sketch, "E489", {"start": v(-15.95, 1.3) * mm, "end": v(-15.51, 1.05) * mm});
            skLineSegment(sketch, "E490", {"start": v(-15.51, 1.05) * mm, "end": v(-15.08, 0.83) * mm});
            skLineSegment(sketch, "E491", {"start": v(-15.08, 0.83) * mm, "end": v(-14.64, 0.65) * mm});
            skLineSegment(sketch, "E492", {"start": v(-14.64, 0.65) * mm, "end": v(-14.19, 0.54) * mm});
            skLineSegment(sketch, "E493", {"start": v(-14.19, 0.54) * mm, "end": v(-13.74, 0.51) * mm});
            skLineSegment(sketch, "E494", {"start": v(-13.74, 0.51) * mm, "end": v(-13.75, 0) * mm});
            skLineSegment(sketch, "E495", {"start": v(-13.75, 0) * mm, "end": v(-13.74, -0.51) * mm});
            skLineSegment(sketch, "E496", {"start": v(-13.74, -0.51) * mm, "end": v(-14.19, -0.54) * mm});
            skLineSegment(sketch, "E497", {"start": v(-14.19, -0.54) * mm, "end": v(-14.64, -0.65) * mm});
            skLineSegment(sketch, "E498", {"start": v(-14.64, -0.65) * mm, "end": v(-15.08, -0.83) * mm});
            skLineSegment(sketch, "E499", {"start": v(-15.08, -0.83) * mm, "end": v(-15.51, -1.05) * mm});
            skLineSegment(sketch, "E500", {"start": v(-15.51, -1.05) * mm, "end": v(-15.95, -1.3) * mm});
            skLineSegment(sketch, "E501", {"start": v(-15.95, -1.3) * mm, "end": v(-15.91, -1.67) * mm});
            skLineSegment(sketch, "E502", {"start": v(-15.91, -1.67) * mm, "end": v(-15.87, -2.04) * mm});
            skLineSegment(sketch, "E503", {"start": v(-15.87, -2.04) * mm, "end": v(-15.4, -2.2) * mm});
            skLineSegment(sketch, "E504", {"start": v(-15.4, -2.2) * mm, "end": v(-14.92, -2.33) * mm});
            skLineSegment(sketch, "E505", {"start": v(-14.92, -2.33) * mm, "end": v(-14.45, -2.4) * mm});
            skLineSegment(sketch, "E506", {"start": v(-14.45, -2.4) * mm, "end": v(-14, -2.42) * mm});
            skLineSegment(sketch, "E507", {"start": v(-14, -2.42) * mm, "end": v(-13.55, -2.35) * mm});
            skLineSegment(sketch, "E508", {"start": v(-13.55, -2.35) * mm, "end": v(-13.45, -2.86) * mm});
            skLineSegment(sketch, "E509", {"start": v(-13.45, -2.86) * mm, "end": v(-13.33, -3.36) * mm});
            skLineSegment(sketch, "E510", {"start": v(-13.33, -3.36) * mm, "end": v(-13.77, -3.48) * mm});
            skLineSegment(sketch, "E511", {"start": v(-13.77, -3.48) * mm, "end": v(-14.18, -3.68) * mm});
            skLineSegment(sketch, "E512", {"start": v(-14.18, -3.68) * mm, "end": v(-14.58, -3.94) * mm});
            skLineSegment(sketch, "E513", {"start": v(-14.58, -3.94) * mm, "end": v(-14.96, -4.25) * mm});
            skLineSegment(sketch, "E514", {"start": v(-14.96, -4.25) * mm, "end": v(-15.33, -4.6) * mm});
            skLineSegment(sketch, "E515", {"start": v(-15.33, -4.6) * mm, "end": v(-15.22, -4.94) * mm});
            skLineSegment(sketch, "E516", {"start": v(-15.22, -4.94) * mm, "end": v(-15.1, -5.3) * mm});
            skLineSegment(sketch, "E517", {"start": v(-15.1, -5.3) * mm, "end": v(-14.6, -5.35) * mm});
            skLineSegment(sketch, "E518", {"start": v(-14.6, -5.35) * mm, "end": v(-14.11, -5.38) * mm});
            skLineSegment(sketch, "E519", {"start": v(-14.11, -5.38) * mm, "end": v(-13.64, -5.35) * mm});
            skLineSegment(sketch, "E520", {"start": v(-13.64, -5.35) * mm, "end": v(-13.18, -5.28) * mm});
            skLineSegment(sketch, "E521", {"start": v(-13.18, -5.28) * mm, "end": v(-12.76, -5.12) * mm});
            skLineSegment(sketch, "E522", {"start": v(-12.76, -5.12) * mm, "end": v(-12.56, -5.6) * mm});
            skLineSegment(sketch, "E523", {"start": v(-12.56, -5.6) * mm, "end": v(-12.34, -6.06) * mm});
            skLineSegment(sketch, "E524", {"start": v(-12.34, -6.06) * mm, "end": v(-12.74, -6.27) * mm});
            skLineSegment(sketch, "E525", {"start": v(-12.74, -6.27) * mm, "end": v(-13.1, -6.55) * mm});
            skLineSegment(sketch, "E526", {"start": v(-13.1, -6.55) * mm, "end": v(-13.44, -6.89) * mm});
            skLineSegment(sketch, "E527", {"start": v(-13.44, -6.89) * mm, "end": v(-13.75, -7.27) * mm});
            skLineSegment(sketch, "E528", {"start": v(-13.75, -7.27) * mm, "end": v(-14.04, -7.68) * mm});
            skLineSegment(sketch, "E529", {"start": v(-14.04, -7.68) * mm, "end": v(-13.86, -8) * mm});
            skLineSegment(sketch, "E530", {"start": v(-13.86, -8) * mm, "end": v(-13.67, -8.32) * mm});
            skLineSegment(sketch, "E531", {"start": v(-13.67, -8.32) * mm, "end": v(-13.17, -8.27) * mm});
            skLineSegment(sketch, "E532", {"start": v(-13.17, -8.27) * mm, "end": v(-12.68, -8.2) * mm});
            skLineSegment(sketch, "E533", {"start": v(-12.68, -8.2) * mm, "end": v(-12.22, -8.07) * mm});
            skLineSegment(sketch, "E534", {"start": v(-12.22, -8.07) * mm, "end": v(-11.8, -7.9) * mm});
            skLineSegment(sketch, "E535", {"start": v(-11.8, -7.9) * mm, "end": v(-11.42, -7.66) * mm});
            skLineSegment(sketch, "E536", {"start": v(-11.42, -7.66) * mm, "end": v(-11.12, -8.08) * mm});
            skLineSegment(sketch, "E537", {"start": v(-11.12, -8.08) * mm, "end": v(-10.81, -8.5) * mm});
            skLineSegment(sketch, "E538", {"start": v(-10.81, -8.5) * mm, "end": v(-11.16, -8.78) * mm});
            skLineSegment(sketch, "E539", {"start": v(-11.16, -8.78) * mm, "end": v(-11.46, -9.13) * mm});
            skLineSegment(sketch, "E540", {"start": v(-11.46, -9.13) * mm, "end": v(-11.71, -9.53) * mm});
            skLineSegment(sketch, "E541", {"start": v(-11.71, -9.53) * mm, "end": v(-11.94, -9.97) * mm});
            skLineSegment(sketch, "E542", {"start": v(-11.94, -9.97) * mm, "end": v(-12.13, -10.43) * mm});
            skLineSegment(sketch, "E543", {"start": v(-12.13, -10.43) * mm, "end": v(-11.9, -10.7) * mm});
            skLineSegment(sketch, "E544", {"start": v(-11.9, -10.7) * mm, "end": v(-11.64, -10.98) * mm});
            skLineSegment(sketch, "E545", {"start": v(-11.64, -10.98) * mm, "end": v(-11.16, -10.83) * mm});
            skLineSegment(sketch, "E546", {"start": v(-11.16, -10.83) * mm, "end": v(-10.7, -10.65) * mm});
            skLineSegment(sketch, "E547", {"start": v(-10.7, -10.65) * mm, "end": v(-10.28, -10.44) * mm});
            skLineSegment(sketch, "E548", {"start": v(-10.28, -10.44) * mm, "end": v(-9.9, -10.18) * mm});
            skLineSegment(sketch, "E549", {"start": v(-9.9, -10.18) * mm, "end": v(-9.58, -9.87) * mm});
            skLineSegment(sketch, "E550", {"start": v(-9.58, -9.87) * mm, "end": v(-9.2, -10.22) * mm});
            skLineSegment(sketch, "E551", {"start": v(-9.2, -10.22) * mm, "end": v(-8.81, -10.56) * mm});
            skLineSegment(sketch, "E552", {"start": v(-8.81, -10.56) * mm, "end": v(-9.1, -10.9) * mm});
            skLineSegment(sketch, "E553", {"start": v(-9.1, -10.9) * mm, "end": v(-9.3, -11.31) * mm});
            skLineSegment(sketch, "E554", {"start": v(-9.3, -11.31) * mm, "end": v(-9.47, -11.76) * mm});
            skLineSegment(sketch, "E555", {"start": v(-9.47, -11.76) * mm, "end": v(-9.6, -12.23) * mm});
            skLineSegment(sketch, "E556", {"start": v(-9.6, -12.23) * mm, "end": v(-9.7, -12.72) * mm});
            skLineSegment(sketch, "E557", {"start": v(-9.7, -12.72) * mm, "end": v(-9.4, -12.94) * mm});
            skLineSegment(sketch, "E558", {"start": v(-9.4, -12.94) * mm, "end": v(-9.1, -13.16) * mm});
            skLineSegment(sketch, "E559", {"start": v(-9.1, -13.16) * mm, "end": v(-8.66, -12.91) * mm});
            skLineSegment(sketch, "E560", {"start": v(-8.66, -12.91) * mm, "end": v(-8.26, -12.64) * mm});
            skLineSegment(sketch, "E561", {"start": v(-8.26, -12.64) * mm, "end": v(-7.88, -12.35) * mm});
            skLineSegment(sketch, "E562", {"start": v(-7.88, -12.35) * mm, "end": v(-7.56, -12.02) * mm});
            skLineSegment(sketch, "E563", {"start": v(-7.56, -12.02) * mm, "end": v(-7.32, -11.64) * mm});
            skLineSegment(sketch, "E564", {"start": v(-7.32, -11.64) * mm, "end": v(-6.88, -11.9) * mm});
            skLineSegment(sketch, "E565", {"start": v(-6.88, -11.9) * mm, "end": v(-6.42, -12.16) * mm});
            skLineSegment(sketch, "E566", {"start": v(-6.42, -12.16) * mm, "end": v(-6.63, -12.56) * mm});
            skLineSegment(sketch, "E567", {"start": v(-6.63, -12.56) * mm, "end": v(-6.75, -13) * mm});
            skLineSegment(sketch, "E568", {"start": v(-6.75, -13) * mm, "end": v(-6.82, -13.47) * mm});
            skLineSegment(sketch, "E569", {"start": v(-6.82, -13.47) * mm, "end": v(-6.85, -13.96) * mm});
            skLineSegment(sketch, "E570", {"start": v(-6.85, -13.96) * mm, "end": v(-6.84, -14.46) * mm});
            skLineSegment(sketch, "E571", {"start": v(-6.84, -14.46) * mm, "end": v(-6.5, -14.62) * mm});
            skLineSegment(sketch, "E572", {"start": v(-6.5, -14.62) * mm, "end": v(-6.17, -14.76) * mm});
            skLineSegment(sketch, "E573", {"start": v(-6.17, -14.76) * mm, "end": v(-5.79, -14.43) * mm});
            skLineSegment(sketch, "E574", {"start": v(-5.79, -14.43) * mm, "end": v(-5.45, -14.08) * mm});
            skLineSegment(sketch, "E575", {"start": v(-5.45, -14.08) * mm, "end": v(-5.14, -13.72) * mm});
            skLineSegment(sketch, "E576", {"start": v(-5.14, -13.72) * mm, "end": v(-4.9, -13.33) * mm});
            skLineSegment(sketch, "E577", {"start": v(-4.9, -13.33) * mm, "end": v(-4.74, -12.9) * mm});
            skLineSegment(sketch, "E578", {"start": v(-4.74, -12.9) * mm, "end": v(-4.25, -13.08) * mm});
            skLineSegment(sketch, "E579", {"start": v(-4.25, -13.08) * mm, "end": v(-3.76, -13.23) * mm});
            skLineSegment(sketch, "E580", {"start": v(-3.76, -13.23) * mm, "end": v(-3.87, -13.66) * mm});
            skLineSegment(sketch, "E581", {"start": v(-3.87, -13.66) * mm, "end": v(-3.9, -14.12) * mm});
            skLineSegment(sketch, "E582", {"start": v(-3.9, -14.12) * mm, "end": v(-3.87, -14.6) * mm});
            skLineSegment(sketch, "E583", {"start": v(-3.87, -14.6) * mm, "end": v(-3.8, -15.08) * mm});
            skLineSegment(sketch, "E584", {"start": v(-3.8, -15.08) * mm, "end": v(-3.69, -15.57) * mm});
            skLineSegment(sketch, "E585", {"start": v(-3.69, -15.57) * mm, "end": v(-3.33, -15.65) * mm});
            skLineSegment(sketch, "E586", {"start": v(-3.33, -15.65) * mm, "end": v(-2.97, -15.72) * mm});
            skLineSegment(sketch, "E587", {"start": v(-2.97, -15.72) * mm, "end": v(-2.66, -15.32) * mm});
            skLineSegment(sketch, "E588", {"start": v(-2.66, -15.32) * mm, "end": v(-2.4, -14.9) * mm});
            skLineSegment(sketch, "E589", {"start": v(-2.4, -14.9) * mm, "end": v(-2.18, -14.49) * mm});
            skLineSegment(sketch, "E590", {"start": v(-2.18, -14.49) * mm, "end": v(-2.02, -14.06) * mm});
            skLineSegment(sketch, "E591", {"start": v(-2.02, -14.06) * mm, "end": v(-1.95, -13.61) * mm});
            skLineSegment(sketch, "E592", {"start": v(-1.95, -13.61) * mm, "end": v(-1.44, -13.67) * mm});
            skLineSegment(sketch, "E593", {"start": v(-1.44, -13.67) * mm, "end": v(-0.92, -13.72) * mm});
            skLineSegment(sketch, "E594", {"start": v(-0.92, -13.72) * mm, "end": v(-0.95, -14.17) * mm});
            skLineSegment(sketch, "E595", {"start": v(-0.95, -14.17) * mm, "end": v(-0.88, -14.62) * mm});
            skLineSegment(sketch, "E596", {"start": v(-0.88, -14.62) * mm, "end": v(-0.75, -15.08) * mm});
            skLineSegment(sketch, "E597", {"start": v(-0.75, -15.08) * mm, "end": v(-0.58, -15.54) * mm});
            skLineSegment(sketch, "E598", {"start": v(-0.58, -15.54) * mm, "end": v(-0.37, -16) * mm});
            skLineSegment(sketch, "E599", {"start": v(-0.37, -16) * mm, "end": v(0, -16) * mm});
            skLineSegment(sketch, "E600", {"start": v(0, -16) * mm, "end": v(0.37, -16) * mm});
            skLineSegment(sketch, "E601", {"start": v(0.37, -16) * mm, "end": v(0.58, -15.54) * mm});
            skLineSegment(sketch, "E602", {"start": v(0.58, -15.54) * mm, "end": v(0.75, -15.08) * mm});
            skLineSegment(sketch, "E603", {"start": v(0.75, -15.08) * mm, "end": v(0.88, -14.62) * mm});
            skLineSegment(sketch, "E604", {"start": v(0.88, -14.62) * mm, "end": v(0.95, -14.17) * mm});
            skLineSegment(sketch, "E605", {"start": v(0.95, -14.17) * mm, "end": v(0.92, -13.72) * mm});
            skLineSegment(sketch, "E606", {"start": v(0.92, -13.72) * mm, "end": v(1.44, -13.67) * mm});
            skLineSegment(sketch, "E607", {"start": v(1.44, -13.67) * mm, "end": v(1.95, -13.61) * mm});
            skLineSegment(sketch, "E608", {"start": v(1.95, -13.61) * mm, "end": v(2.02, -14.06) * mm});
            skLineSegment(sketch, "E609", {"start": v(2.02, -14.06) * mm, "end": v(2.18, -14.49) * mm});
            skLineSegment(sketch, "E610", {"start": v(2.18, -14.49) * mm, "end": v(2.4, -14.9) * mm});
            skLineSegment(sketch, "E611", {"start": v(2.4, -14.9) * mm, "end": v(2.66, -15.32) * mm});
            skLineSegment(sketch, "E612", {"start": v(2.66, -15.32) * mm, "end": v(2.97, -15.72) * mm});
            skLineSegment(sketch, "E613", {"start": v(2.97, -15.72) * mm, "end": v(3.33, -15.65) * mm});
            skLineSegment(sketch, "E614", {"start": v(3.33, -15.65) * mm, "end": v(3.69, -15.57) * mm});
            skLineSegment(sketch, "E615", {"start": v(3.69, -15.57) * mm, "end": v(3.8, -15.08) * mm});
            skLineSegment(sketch, "E616", {"start": v(3.8, -15.08) * mm, "end": v(3.87, -14.6) * mm});
            skLineSegment(sketch, "E617", {"start": v(3.87, -14.6) * mm, "end": v(3.9, -14.12) * mm});
            skLineSegment(sketch, "E618", {"start": v(3.9, -14.12) * mm, "end": v(3.87, -13.66) * mm});
            skLineSegment(sketch, "E619", {"start": v(3.87, -13.66) * mm, "end": v(3.76, -13.23) * mm});
            skLineSegment(sketch, "E620", {"start": v(3.76, -13.23) * mm, "end": v(4.25, -13.08) * mm});
            skLineSegment(sketch, "E621", {"start": v(4.25, -13.08) * mm, "end": v(4.74, -12.9) * mm});
            skLineSegment(sketch, "E622", {"start": v(4.74, -12.9) * mm, "end": v(4.9, -13.33) * mm});
            skLineSegment(sketch, "E623", {"start": v(4.9, -13.33) * mm, "end": v(5.14, -13.72) * mm});
            skLineSegment(sketch, "E624", {"start": v(5.14, -13.72) * mm, "end": v(5.45, -14.08) * mm});
            skLineSegment(sketch, "E625", {"start": v(5.45, -14.08) * mm, "end": v(5.79, -14.43) * mm});
            skLineSegment(sketch, "E626", {"start": v(5.79, -14.43) * mm, "end": v(6.17, -14.76) * mm});
            skLineSegment(sketch, "E627", {"start": v(6.17, -14.76) * mm, "end": v(6.5, -14.62) * mm});
            skLineSegment(sketch, "E628", {"start": v(6.5, -14.62) * mm, "end": v(6.84, -14.46) * mm});
            skLineSegment(sketch, "E629", {"start": v(6.84, -14.46) * mm, "end": v(6.85, -13.96) * mm});
            skLineSegment(sketch, "E630", {"start": v(6.85, -13.96) * mm, "end": v(6.82, -13.47) * mm});
            skLineSegment(sketch, "E631", {"start": v(6.82, -13.47) * mm, "end": v(6.75, -13) * mm});
            skLineSegment(sketch, "E632", {"start": v(6.75, -13) * mm, "end": v(6.63, -12.56) * mm});
            skLineSegment(sketch, "E633", {"start": v(6.63, -12.56) * mm, "end": v(6.42, -12.16) * mm});
            skLineSegment(sketch, "E634", {"start": v(6.42, -12.16) * mm, "end": v(6.88, -11.9) * mm});
            skLineSegment(sketch, "E635", {"start": v(6.88, -11.9) * mm, "end": v(7.32, -11.64) * mm});
            skLineSegment(sketch, "E636", {"start": v(7.32, -11.64) * mm, "end": v(7.56, -12.02) * mm});
            skLineSegment(sketch, "E637", {"start": v(7.56, -12.02) * mm, "end": v(7.88, -12.35) * mm});
            skLineSegment(sketch, "E638", {"start": v(7.88, -12.35) * mm, "end": v(8.26, -12.64) * mm});
            skLineSegment(sketch, "E639", {"start": v(8.26, -12.64) * mm, "end": v(8.66, -12.91) * mm});
            skLineSegment(sketch, "E640", {"start": v(8.66, -12.91) * mm, "end": v(9.1, -13.16) * mm});
            skLineSegment(sketch, "E641", {"start": v(9.1, -13.16) * mm, "end": v(9.4, -12.94) * mm});
            skLineSegment(sketch, "E642", {"start": v(9.4, -12.94) * mm, "end": v(9.7, -12.72) * mm});
            skLineSegment(sketch, "E643", {"start": v(9.7, -12.72) * mm, "end": v(9.6, -12.23) * mm});
            skLineSegment(sketch, "E644", {"start": v(9.6, -12.23) * mm, "end": v(9.47, -11.76) * mm});
            skLineSegment(sketch, "E645", {"start": v(9.47, -11.76) * mm, "end": v(9.3, -11.31) * mm});
            skLineSegment(sketch, "E646", {"start": v(9.3, -11.31) * mm, "end": v(9.1, -10.9) * mm});
            skLineSegment(sketch, "E647", {"start": v(9.1, -10.9) * mm, "end": v(8.81, -10.56) * mm});
            skLineSegment(sketch, "E648", {"start": v(8.81, -10.56) * mm, "end": v(9.2, -10.22) * mm});
            skLineSegment(sketch, "E649", {"start": v(9.2, -10.22) * mm, "end": v(9.58, -9.87) * mm});
            skLineSegment(sketch, "E650", {"start": v(9.58, -9.87) * mm, "end": v(9.9, -10.18) * mm});
            skLineSegment(sketch, "E651", {"start": v(9.9, -10.18) * mm, "end": v(10.28, -10.44) * mm});
            skLineSegment(sketch, "E652", {"start": v(10.28, -10.44) * mm, "end": v(10.7, -10.65) * mm});
            skLineSegment(sketch, "E653", {"start": v(10.7, -10.65) * mm, "end": v(11.16, -10.83) * mm});
            skLineSegment(sketch, "E654", {"start": v(11.16, -10.83) * mm, "end": v(11.64, -10.98) * mm});
            skLineSegment(sketch, "E655", {"start": v(11.64, -10.98) * mm, "end": v(11.9, -10.7) * mm});
            skLineSegment(sketch, "E656", {"start": v(11.9, -10.7) * mm, "end": v(12.13, -10.43) * mm});
            skLineSegment(sketch, "E657", {"start": v(12.13, -10.43) * mm, "end": v(11.94, -9.97) * mm});
            skLineSegment(sketch, "E658", {"start": v(11.94, -9.97) * mm, "end": v(11.71, -9.53) * mm});
            skLineSegment(sketch, "E659", {"start": v(11.71, -9.53) * mm, "end": v(11.46, -9.13) * mm});
            skLineSegment(sketch, "E660", {"start": v(11.46, -9.13) * mm, "end": v(11.16, -8.78) * mm});
            skLineSegment(sketch, "E661", {"start": v(11.16, -8.78) * mm, "end": v(10.81, -8.5) * mm});
            skLineSegment(sketch, "E662", {"start": v(10.81, -8.5) * mm, "end": v(11.12, -8.08) * mm});
            skLineSegment(sketch, "E663", {"start": v(11.12, -8.08) * mm, "end": v(11.42, -7.66) * mm});
            skLineSegment(sketch, "E664", {"start": v(11.42, -7.66) * mm, "end": v(11.8, -7.9) * mm});
            skLineSegment(sketch, "E665", {"start": v(11.8, -7.9) * mm, "end": v(12.22, -8.07) * mm});
            skLineSegment(sketch, "E666", {"start": v(12.22, -8.07) * mm, "end": v(12.68, -8.2) * mm});
            skLineSegment(sketch, "E667", {"start": v(12.68, -8.2) * mm, "end": v(13.17, -8.27) * mm});
            skLineSegment(sketch, "E668", {"start": v(13.17, -8.27) * mm, "end": v(13.67, -8.32) * mm});
            skLineSegment(sketch, "E669", {"start": v(13.67, -8.32) * mm, "end": v(13.86, -8) * mm});
            skLineSegment(sketch, "E670", {"start": v(13.86, -8) * mm, "end": v(14.04, -7.68) * mm});
            skLineSegment(sketch, "E671", {"start": v(14.04, -7.68) * mm, "end": v(13.75, -7.27) * mm});
            skLineSegment(sketch, "E672", {"start": v(13.75, -7.27) * mm, "end": v(13.44, -6.89) * mm});
            skLineSegment(sketch, "E673", {"start": v(13.44, -6.89) * mm, "end": v(13.1, -6.55) * mm});
            skLineSegment(sketch, "E674", {"start": v(13.1, -6.55) * mm, "end": v(12.74, -6.27) * mm});
            skLineSegment(sketch, "E675", {"start": v(12.74, -6.27) * mm, "end": v(12.34, -6.06) * mm});
            skLineSegment(sketch, "E676", {"start": v(12.34, -6.06) * mm, "end": v(12.56, -5.6) * mm});
            skLineSegment(sketch, "E677", {"start": v(12.56, -5.6) * mm, "end": v(12.76, -5.12) * mm});
            skLineSegment(sketch, "E678", {"start": v(12.76, -5.12) * mm, "end": v(13.18, -5.28) * mm});
            skLineSegment(sketch, "E679", {"start": v(13.18, -5.28) * mm, "end": v(13.64, -5.35) * mm});
            skLineSegment(sketch, "E680", {"start": v(13.64, -5.35) * mm, "end": v(14.11, -5.38) * mm});
            skLineSegment(sketch, "E681", {"start": v(14.11, -5.38) * mm, "end": v(14.6, -5.35) * mm});
            skLineSegment(sketch, "E682", {"start": v(14.6, -5.35) * mm, "end": v(15.1, -5.3) * mm});
            skLineSegment(sketch, "E683", {"start": v(15.1, -5.3) * mm, "end": v(15.22, -4.94) * mm});
            skLineSegment(sketch, "E684", {"start": v(15.22, -4.94) * mm, "end": v(15.33, -4.6) * mm});
            skLineSegment(sketch, "E685", {"start": v(15.33, -4.6) * mm, "end": v(14.96, -4.25) * mm});
            skLineSegment(sketch, "E686", {"start": v(14.96, -4.25) * mm, "end": v(14.58, -3.94) * mm});
            skLineSegment(sketch, "E687", {"start": v(14.58, -3.94) * mm, "end": v(14.18, -3.68) * mm});
            skLineSegment(sketch, "E688", {"start": v(14.18, -3.68) * mm, "end": v(13.77, -3.48) * mm});
            skLineSegment(sketch, "E689", {"start": v(13.77, -3.48) * mm, "end": v(13.33, -3.36) * mm});
            skLineSegment(sketch, "E690", {"start": v(13.33, -3.36) * mm, "end": v(13.45, -2.86) * mm});
            skLineSegment(sketch, "E691", {"start": v(13.45, -2.86) * mm, "end": v(13.55, -2.35) * mm});
            skLineSegment(sketch, "E692", {"start": v(13.55, -2.35) * mm, "end": v(14, -2.42) * mm});
            skLineSegment(sketch, "E693", {"start": v(14, -2.42) * mm, "end": v(14.45, -2.4) * mm});
            skLineSegment(sketch, "E694", {"start": v(14.45, -2.4) * mm, "end": v(14.92, -2.33) * mm});
            skLineSegment(sketch, "E695", {"start": v(14.92, -2.33) * mm, "end": v(15.4, -2.2) * mm});
            skLineSegment(sketch, "E696", {"start": v(15.4, -2.2) * mm, "end": v(15.87, -2.04) * mm});
            skLineSegment(sketch, "E697", {"start": v(15.87, -2.04) * mm, "end": v(15.91, -1.67) * mm});
            skLineSegment(sketch, "E698", {"start": v(15.91, -1.67) * mm, "end": v(15.95, -1.3) * mm});
            skLineSegment(sketch, "E699", {"start": v(15.95, -1.3) * mm, "end": v(15.51, -1.05) * mm});
            skLineSegment(sketch, "E700", {"start": v(15.51, -1.05) * mm, "end": v(15.08, -0.83) * mm});
            skLineSegment(sketch, "E701", {"start": v(15.08, -0.83) * mm, "end": v(14.64, -0.65) * mm});
            skLineSegment(sketch, "E702", {"start": v(14.64, -0.65) * mm, "end": v(14.19, -0.54) * mm});
            skLineSegment(sketch, "E703", {"start": v(14.19, -0.54) * mm, "end": v(13.74, -0.51) * mm});
            skLineSegment(sketch, "E704", {"start": v(13.75, 0) * mm, "end": v(13.74, -0.51) * mm});
            skSolve(sketch);
        }
        {
            var Q0;
            Q0 = qSketchRegion(id + "F4", true);
            extrude(context, id + "F5", {"entities" : qUnion([Q0]), "oppositeDirection" : true, "depth" : 5 * mm, "offsetDistance" : 25 * mm});
        }
        {
            var Q0;
            Q0=makeQuery(id+"F5.opExtrude","CAP_FACE",FACE,{"disambiguationData":[OSD([sQuery(id+"F4.wireOp",EDGE,"E285"),sQuery(id+"F4.wireOp",EDGE,"E286"),sQuery(id+"F4.wireOp",EDGE,"E287"),sQuery(id+"F4.wireOp",EDGE,"E288"),sQuery(id+"F4.wireOp",EDGE,"E289"),sQuery(id+"F4.wireOp",EDGE,"E290"),sQuery(id+"F4.wireOp",EDGE,"E291"),sQuery(id+"F4.wireOp",EDGE,"E292"),sQuery(id+"F4.wireOp",EDGE,"E293"),sQuery(id+"F4.wireOp",EDGE,"E294"),sQuery(id+"F4.wireOp",EDGE,"E295"),sQuery(id+"F4.wireOp",EDGE,"E296"),sQuery(id+"F4.wireOp",EDGE,"E297"),sQuery(id+"F4.wireOp",EDGE,"E298"),sQuery(id+"F4.wireOp",EDGE,"E299"),sQuery(id+"F4.wireOp",EDGE,"E300"),sQuery(id+"F4.wireOp",EDGE,"E301"),sQuery(id+"F4.wireOp",EDGE,"E302"),sQuery(id+"F4.wireOp",EDGE,"E303"),sQuery(id+"F4.wireOp",EDGE,"E304"),sQuery(id+"F4.wireOp",EDGE,"E305"),sQuery(id+"F4.wireOp",EDGE,"E306"),sQuery(id+"F4.wireOp",EDGE,"E307"),sQuery(id+"F4.wireOp",EDGE,"E308"),sQuery(id+"F4.wireOp",EDGE,"E309"),sQuery(id+"F4.wireOp",EDGE,"E310"),sQuery(id+"F4.wireOp",EDGE,"E311"),sQuery(id+"F4.wireOp",EDGE,"E312"),sQuery(id+"F4.wireOp",EDGE,"E313"),sQuery(id+"F4.wireOp",EDGE,"E314"),sQuery(id+"F4.wireOp",EDGE,"E315"),sQuery(id+"F4.wireOp",EDGE,"E316"),sQuery(id+"F4.wireOp",EDGE,"E317"),sQuery(id+"F4.wireOp",EDGE,"E318"),sQuery(id+"F4.wireOp",EDGE,"E319"),sQuery(id+"F4.wireOp",EDGE,"E320"),sQuery(id+"F4.wireOp",EDGE,"E321"),sQuery(id+"F4.wireOp",EDGE,"E322"),sQuery(id+"F4.wireOp",EDGE,"E323"),sQuery(id+"F4.wireOp",EDGE,"E324"),sQuery(id+"F4.wireOp",EDGE,"E325"),sQuery(id+"F4.wireOp",EDGE,"E326"),sQuery(id+"F4.wireOp",EDGE,"E327"),sQuery(id+"F4.wireOp",EDGE,"E328"),sQuery(id+"F4.wireOp",EDGE,"E329"),sQuery(id+"F4.wireOp",EDGE,"E330"),sQuery(id+"F4.wireOp",EDGE,"E331"),sQuery(id+"F4.wireOp",EDGE,"E332"),sQuery(id+"F4.wireOp",EDGE,"E333"),sQuery(id+"F4.wireOp",EDGE,"E334"),sQuery(id+"F4.wireOp",EDGE,"E335"),sQuery(id+"F4.wireOp",EDGE,"E336"),sQuery(id+"F4.wireOp",EDGE,"E337"),sQuery(id+"F4.wireOp",EDGE,"E338"),sQuery(id+"F4.wireOp",EDGE,"E339"),sQuery(id+"F4.wireOp",EDGE,"E340"),sQuery(id+"F4.wireOp",EDGE,"E341"),sQuery(id+"F4.wireOp",EDGE,"E342"),sQuery(id+"F4.wireOp",EDGE,"E343"),sQuery(id+"F4.wireOp",EDGE,"E344"),sQuery(id+"F4.wireOp",EDGE,"E345"),sQuery(id+"F4.wireOp",EDGE,"E346"),sQuery(id+"F4.wireOp",EDGE,"E347"),sQuery(id+"F4.wireOp",EDGE,"E348"),sQuery(id+"F4.wireOp",EDGE,"E349"),sQuery(id+"F4.wireOp",EDGE,"E350"),sQuery(id+"F4.wireOp",EDGE,"E351"),sQuery(id+"F4.wireOp",EDGE,"E352"),sQuery(id+"F4.wireOp",EDGE,"E353"),sQuery(id+"F4.wireOp",EDGE,"E354"),sQuery(id+"F4.wireOp",EDGE,"E355"),sQuery(id+"F4.wireOp",EDGE,"E356"),sQuery(id+"F4.wireOp",EDGE,"E357"),sQuery(id+"F4.wireOp",EDGE,"E358"),sQuery(id+"F4.wireOp",EDGE,"E359"),sQuery(id+"F4.wireOp",EDGE,"E360"),sQuery(id+"F4.wireOp",EDGE,"E361"),sQuery(id+"F4.wireOp",EDGE,"E362"),sQuery(id+"F4.wireOp",EDGE,"E363"),sQuery(id+"F4.wireOp",EDGE,"E364"),sQuery(id+"F4.wireOp",EDGE,"E365"),sQuery(id+"F4.wireOp",EDGE,"E366"),sQuery(id+"F4.wireOp",EDGE,"E367"),sQuery(id+"F4.wireOp",EDGE,"E368"),sQuery(id+"F4.wireOp",EDGE,"E369"),sQuery(id+"F4.wireOp",EDGE,"E370"),sQuery(id+"F4.wireOp",EDGE,"E371"),sQuery(id+"F4.wireOp",EDGE,"E372"),sQuery(id+"F4.wireOp",EDGE,"E373"),sQuery(id+"F4.wireOp",EDGE,"E374"),sQuery(id+"F4.wireOp",EDGE,"E375"),sQuery(id+"F4.wireOp",EDGE,"E376"),sQuery(id+"F4.wireOp",EDGE,"E377"),sQuery(id+"F4.wireOp",EDGE,"E378"),sQuery(id+"F4.wireOp",EDGE,"E379"),sQuery(id+"F4.wireOp",EDGE,"E380"),sQuery(id+"F4.wireOp",EDGE,"E381"),sQuery(id+"F4.wireOp",EDGE,"E382"),sQuery(id+"F4.wireOp",EDGE,"E383"),sQuery(id+"F4.wireOp",EDGE,"E384"),sQuery(id+"F4.wireOp",EDGE,"E385"),sQuery(id+"F4.wireOp",EDGE,"E386"),sQuery(id+"F4.wireOp",EDGE,"E387"),sQuery(id+"F4.wireOp",EDGE,"E388"),sQuery(id+"F4.wireOp",EDGE,"E389"),sQuery(id+"F4.wireOp",EDGE,"E390"),sQuery(id+"F4.wireOp",EDGE,"E391"),sQuery(id+"F4.wireOp",EDGE,"E392"),sQuery(id+"F4.wireOp",EDGE,"E393"),sQuery(id+"F4.wireOp",EDGE,"E394"),sQuery(id+"F4.wireOp",EDGE,"E395"),sQuery(id+"F4.wireOp",EDGE,"E396"),sQuery(id+"F4.wireOp",EDGE,"E397"),sQuery(id+"F4.wireOp",EDGE,"E398"),sQuery(id+"F4.wireOp",EDGE,"E399"),sQuery(id+"F4.wireOp",EDGE,"E400"),sQuery(id+"F4.wireOp",EDGE,"E401"),sQuery(id+"F4.wireOp",EDGE,"E402"),sQuery(id+"F4.wireOp",EDGE,"E403"),sQuery(id+"F4.wireOp",EDGE,"E404"),sQuery(id+"F4.wireOp",EDGE,"E405"),sQuery(id+"F4.wireOp",EDGE,"E406"),sQuery(id+"F4.wireOp",EDGE,"E407"),sQuery(id+"F4.wireOp",EDGE,"E408"),sQuery(id+"F4.wireOp",EDGE,"E409"),sQuery(id+"F4.wireOp",EDGE,"E410"),sQuery(id+"F4.wireOp",EDGE,"E411"),sQuery(id+"F4.wireOp",EDGE,"E412"),sQuery(id+"F4.wireOp",EDGE,"E413"),sQuery(id+"F4.wireOp",EDGE,"E414"),sQuery(id+"F4.wireOp",EDGE,"E415"),sQuery(id+"F4.wireOp",EDGE,"E416"),sQuery(id+"F4.wireOp",EDGE,"E417"),sQuery(id+"F4.wireOp",EDGE,"E418"),sQuery(id+"F4.wireOp",EDGE,"E419"),sQuery(id+"F4.wireOp",EDGE,"E420"),sQuery(id+"F4.wireOp",EDGE,"E421"),sQuery(id+"F4.wireOp",EDGE,"E422"),sQuery(id+"F4.wireOp",EDGE,"E423"),sQuery(id+"F4.wireOp",EDGE,"E424"),sQuery(id+"F4.wireOp",EDGE,"E425"),sQuery(id+"F4.wireOp",EDGE,"E426"),sQuery(id+"F4.wireOp",EDGE,"E427"),sQuery(id+"F4.wireOp",EDGE,"E428"),sQuery(id+"F4.wireOp",EDGE,"E429"),sQuery(id+"F4.wireOp",EDGE,"E430"),sQuery(id+"F4.wireOp",EDGE,"E431"),sQuery(id+"F4.wireOp",EDGE,"E432"),sQuery(id+"F4.wireOp",EDGE,"E433"),sQuery(id+"F4.wireOp",EDGE,"E434"),sQuery(id+"F4.wireOp",EDGE,"E435"),sQuery(id+"F4.wireOp",EDGE,"E436"),sQuery(id+"F4.wireOp",EDGE,"E437"),sQuery(id+"F4.wireOp",EDGE,"E438"),sQuery(id+"F4.wireOp",EDGE,"E439"),sQuery(id+"F4.wireOp",EDGE,"E440"),sQuery(id+"F4.wireOp",EDGE,"E441"),sQuery(id+"F4.wireOp",EDGE,"E442"),sQuery(id+"F4.wireOp",EDGE,"E443"),sQuery(id+"F4.wireOp",EDGE,"E444"),sQuery(id+"F4.wireOp",EDGE,"E445"),sQuery(id+"F4.wireOp",EDGE,"E446"),sQuery(id+"F4.wireOp",EDGE,"E447"),sQuery(id+"F4.wireOp",EDGE,"E448"),sQuery(id+"F4.wireOp",EDGE,"E449"),sQuery(id+"F4.wireOp",EDGE,"E450"),sQuery(id+"F4.wireOp",EDGE,"E451"),sQuery(id+"F4.wireOp",EDGE,"E452"),sQuery(id+"F4.wireOp",EDGE,"E453"),sQuery(id+"F4.wireOp",EDGE,"E454"),sQuery(id+"F4.wireOp",EDGE,"E455"),sQuery(id+"F4.wireOp",EDGE,"E456"),sQuery(id+"F4.wireOp",EDGE,"E457"),sQuery(id+"F4.wireOp",EDGE,"E458"),sQuery(id+"F4.wireOp",EDGE,"E459"),sQuery(id+"F4.wireOp",EDGE,"E460"),sQuery(id+"F4.wireOp",EDGE,"E461"),sQuery(id+"F4.wireOp",EDGE,"E462"),sQuery(id+"F4.wireOp",EDGE,"E463"),sQuery(id+"F4.wireOp",EDGE,"E464"),sQuery(id+"F4.wireOp",EDGE,"E465"),sQuery(id+"F4.wireOp",EDGE,"E466"),sQuery(id+"F4.wireOp",EDGE,"E467"),sQuery(id+"F4.wireOp",EDGE,"E468"),sQuery(id+"F4.wireOp",EDGE,"E469"),sQuery(id+"F4.wireOp",EDGE,"E470"),sQuery(id+"F4.wireOp",EDGE,"E471"),sQuery(id+"F4.wireOp",EDGE,"E472"),sQuery(id+"F4.wireOp",EDGE,"E473"),sQuery(id+"F4.wireOp",EDGE,"E474"),sQuery(id+"F4.wireOp",EDGE,"E475"),sQuery(id+"F4.wireOp",EDGE,"E476"),sQuery(id+"F4.wireOp",EDGE,"E477"),sQuery(id+"F4.wireOp",EDGE,"E478"),sQuery(id+"F4.wireOp",EDGE,"E479"),sQuery(id+"F4.wireOp",EDGE,"E480"),sQuery(id+"F4.wireOp",EDGE,"E481"),sQuery(id+"F4.wireOp",EDGE,"E482"),sQuery(id+"F4.wireOp",EDGE,"E483"),sQuery(id+"F4.wireOp",EDGE,"E484"),sQuery(id+"F4.wireOp",EDGE,"E485"),sQuery(id+"F4.wireOp",EDGE,"E486"),sQuery(id+"F4.wireOp",EDGE,"E487"),sQuery(id+"F4.wireOp",EDGE,"E488"),sQuery(id+"F4.wireOp",EDGE,"E489"),sQuery(id+"F4.wireOp",EDGE,"E490"),sQuery(id+"F4.wireOp",EDGE,"E491"),sQuery(id+"F4.wireOp",EDGE,"E492"),sQuery(id+"F4.wireOp",EDGE,"E493"),sQuery(id+"F4.wireOp",EDGE,"E494"),sQuery(id+"F4.wireOp",EDGE,"E495"),sQuery(id+"F4.wireOp",EDGE,"E496"),sQuery(id+"F4.wireOp",EDGE,"E497"),sQuery(id+"F4.wireOp",EDGE,"E498"),sQuery(id+"F4.wireOp",EDGE,"E499"),sQuery(id+"F4.wireOp",EDGE,"E500"),sQuery(id+"F4.wireOp",EDGE,"E501"),sQuery(id+"F4.wireOp",EDGE,"E502"),sQuery(id+"F4.wireOp",EDGE,"E503"),sQuery(id+"F4.wireOp",EDGE,"E504"),sQuery(id+"F4.wireOp",EDGE,"E505"),sQuery(id+"F4.wireOp",EDGE,"E506"),sQuery(id+"F4.wireOp",EDGE,"E507"),sQuery(id+"F4.wireOp",EDGE,"E508"),sQuery(id+"F4.wireOp",EDGE,"E509"),sQuery(id+"F4.wireOp",EDGE,"E510"),sQuery(id+"F4.wireOp",EDGE,"E511"),sQuery(id+"F4.wireOp",EDGE,"E512"),sQuery(id+"F4.wireOp",EDGE,"E513"),sQuery(id+"F4.wireOp",EDGE,"E514"),sQuery(id+"F4.wireOp",EDGE,"E515"),sQuery(id+"F4.wireOp",EDGE,"E516"),sQuery(id+"F4.wireOp",EDGE,"E517"),sQuery(id+"F4.wireOp",EDGE,"E518"),sQuery(id+"F4.wireOp",EDGE,"E519"),sQuery(id+"F4.wireOp",EDGE,"E520"),sQuery(id+"F4.wireOp",EDGE,"E521"),sQuery(id+"F4.wireOp",EDGE,"E522"),sQuery(id+"F4.wireOp",EDGE,"E523"),sQuery(id+"F4.wireOp",EDGE,"E524"),sQuery(id+"F4.wireOp",EDGE,"E525"),sQuery(id+"F4.wireOp",EDGE,"E526"),sQuery(id+"F4.wireOp",EDGE,"E527"),sQuery(id+"F4.wireOp",EDGE,"E528"),sQuery(id+"F4.wireOp",EDGE,"E529"),sQuery(id+"F4.wireOp",EDGE,"E530"),sQuery(id+"F4.wireOp",EDGE,"E531"),sQuery(id+"F4.wireOp",EDGE,"E532"),sQuery(id+"F4.wireOp",EDGE,"E533"),sQuery(id+"F4.wireOp",EDGE,"E534"),sQuery(id+"F4.wireOp",EDGE,"E535"),sQuery(id+"F4.wireOp",EDGE,"E536"),sQuery(id+"F4.wireOp",EDGE,"E537"),sQuery(id+"F4.wireOp",EDGE,"E538"),sQuery(id+"F4.wireOp",EDGE,"E539"),sQuery(id+"F4.wireOp",EDGE,"E540"),sQuery(id+"F4.wireOp",EDGE,"E541"),sQuery(id+"F4.wireOp",EDGE,"E542"),sQuery(id+"F4.wireOp",EDGE,"E543"),sQuery(id+"F4.wireOp",EDGE,"E544"),sQuery(id+"F4.wireOp",EDGE,"E545"),sQuery(id+"F4.wireOp",EDGE,"E546"),sQuery(id+"F4.wireOp",EDGE,"E547"),sQuery(id+"F4.wireOp",EDGE,"E548"),sQuery(id+"F4.wireOp",EDGE,"E549"),sQuery(id+"F4.wireOp",EDGE,"E550"),sQuery(id+"F4.wireOp",EDGE,"E551"),sQuery(id+"F4.wireOp",EDGE,"E552"),sQuery(id+"F4.wireOp",EDGE,"E553"),sQuery(id+"F4.wireOp",EDGE,"E554"),sQuery(id+"F4.wireOp",EDGE,"E555"),sQuery(id+"F4.wireOp",EDGE,"E556"),sQuery(id+"F4.wireOp",EDGE,"E557"),sQuery(id+"F4.wireOp",EDGE,"E558"),sQuery(id+"F4.wireOp",EDGE,"E559"),sQuery(id+"F4.wireOp",EDGE,"E560"),sQuery(id+"F4.wireOp",EDGE,"E561"),sQuery(id+"F4.wireOp",EDGE,"E562"),sQuery(id+"F4.wireOp",EDGE,"E563"),sQuery(id+"F4.wireOp",EDGE,"E564"),sQuery(id+"F4.wireOp",EDGE,"E565"),sQuery(id+"F4.wireOp",EDGE,"E566"),sQuery(id+"F4.wireOp",EDGE,"E567"),sQuery(id+"F4.wireOp",EDGE,"E568"),sQuery(id+"F4.wireOp",EDGE,"E569"),sQuery(id+"F4.wireOp",EDGE,"E570"),sQuery(id+"F4.wireOp",EDGE,"E571"),sQuery(id+"F4.wireOp",EDGE,"E572"),sQuery(id+"F4.wireOp",EDGE,"E573"),sQuery(id+"F4.wireOp",EDGE,"E574"),sQuery(id+"F4.wireOp",EDGE,"E575"),sQuery(id+"F4.wireOp",EDGE,"E576"),sQuery(id+"F4.wireOp",EDGE,"E577"),sQuery(id+"F4.wireOp",EDGE,"E578"),sQuery(id+"F4.wireOp",EDGE,"E579"),sQuery(id+"F4.wireOp",EDGE,"E580"),sQuery(id+"F4.wireOp",EDGE,"E581"),sQuery(id+"F4.wireOp",EDGE,"E582"),sQuery(id+"F4.wireOp",EDGE,"E583"),sQuery(id+"F4.wireOp",EDGE,"E584"),sQuery(id+"F4.wireOp",EDGE,"E585"),sQuery(id+"F4.wireOp",EDGE,"E586"),sQuery(id+"F4.wireOp",EDGE,"E587"),sQuery(id+"F4.wireOp",EDGE,"E588"),sQuery(id+"F4.wireOp",EDGE,"E589"),sQuery(id+"F4.wireOp",EDGE,"E590"),sQuery(id+"F4.wireOp",EDGE,"E591"),sQuery(id+"F4.wireOp",EDGE,"E592"),sQuery(id+"F4.wireOp",EDGE,"E593"),sQuery(id+"F4.wireOp",EDGE,"E594"),sQuery(id+"F4.wireOp",EDGE,"E595"),sQuery(id+"F4.wireOp",EDGE,"E596"),sQuery(id+"F4.wireOp",EDGE,"E597"),sQuery(id+"F4.wireOp",EDGE,"E598"),sQuery(id+"F4.wireOp",EDGE,"E599"),sQuery(id+"F4.wireOp",EDGE,"E600"),sQuery(id+"F4.wireOp",EDGE,"E601"),sQuery(id+"F4.wireOp",EDGE,"E602"),sQuery(id+"F4.wireOp",EDGE,"E603"),sQuery(id+"F4.wireOp",EDGE,"E604"),sQuery(id+"F4.wireOp",EDGE,"E605"),sQuery(id+"F4.wireOp",EDGE,"E606"),sQuery(id+"F4.wireOp",EDGE,"E607"),sQuery(id+"F4.wireOp",EDGE,"E608"),sQuery(id+"F4.wireOp",EDGE,"E609"),sQuery(id+"F4.wireOp",EDGE,"E610"),sQuery(id+"F4.wireOp",EDGE,"E611"),sQuery(id+"F4.wireOp",EDGE,"E612"),sQuery(id+"F4.wireOp",EDGE,"E613"),sQuery(id+"F4.wireOp",EDGE,"E614"),sQuery(id+"F4.wireOp",EDGE,"E615"),sQuery(id+"F4.wireOp",EDGE,"E616"),sQuery(id+"F4.wireOp",EDGE,"E617"),sQuery(id+"F4.wireOp",EDGE,"E618"),sQuery(id+"F4.wireOp",EDGE,"E619"),sQuery(id+"F4.wireOp",EDGE,"E620"),sQuery(id+"F4.wireOp",EDGE,"E621"),sQuery(id+"F4.wireOp",EDGE,"E622"),sQuery(id+"F4.wireOp",EDGE,"E623"),sQuery(id+"F4.wireOp",EDGE,"E624"),sQuery(id+"F4.wireOp",EDGE,"E625"),sQuery(id+"F4.wireOp",EDGE,"E626"),sQuery(id+"F4.wireOp",EDGE,"E627"),sQuery(id+"F4.wireOp",EDGE,"E628"),sQuery(id+"F4.wireOp",EDGE,"E629"),sQuery(id+"F4.wireOp",EDGE,"E630"),sQuery(id+"F4.wireOp",EDGE,"E631"),sQuery(id+"F4.wireOp",EDGE,"E632"),sQuery(id+"F4.wireOp",EDGE,"E633"),sQuery(id+"F4.wireOp",EDGE,"E634"),sQuery(id+"F4.wireOp",EDGE,"E635"),sQuery(id+"F4.wireOp",EDGE,"E636"),sQuery(id+"F4.wireOp",EDGE,"E637"),sQuery(id+"F4.wireOp",EDGE,"E638"),sQuery(id+"F4.wireOp",EDGE,"E639"),sQuery(id+"F4.wireOp",EDGE,"E640"),sQuery(id+"F4.wireOp",EDGE,"E641"),sQuery(id+"F4.wireOp",EDGE,"E642"),sQuery(id+"F4.wireOp",EDGE,"E643"),sQuery(id+"F4.wireOp",EDGE,"E644"),sQuery(id+"F4.wireOp",EDGE,"E645"),sQuery(id+"F4.wireOp",EDGE,"E646"),sQuery(id+"F4.wireOp",EDGE,"E647"),sQuery(id+"F4.wireOp",EDGE,"E648"),sQuery(id+"F4.wireOp",EDGE,"E649"),sQuery(id+"F4.wireOp",EDGE,"E650"),sQuery(id+"F4.wireOp",EDGE,"E651"),sQuery(id+"F4.wireOp",EDGE,"E652"),sQuery(id+"F4.wireOp",EDGE,"E653"),sQuery(id+"F4.wireOp",EDGE,"E654"),sQuery(id+"F4.wireOp",EDGE,"E655"),sQuery(id+"F4.wireOp",EDGE,"E656"),sQuery(id+"F4.wireOp",EDGE,"E657"),sQuery(id+"F4.wireOp",EDGE,"E658"),sQuery(id+"F4.wireOp",EDGE,"E659"),sQuery(id+"F4.wireOp",EDGE,"E660"),sQuery(id+"F4.wireOp",EDGE,"E661"),sQuery(id+"F4.wireOp",EDGE,"E662"),sQuery(id+"F4.wireOp",EDGE,"E663"),sQuery(id+"F4.wireOp",EDGE,"E664"),sQuery(id+"F4.wireOp",EDGE,"E665"),sQuery(id+"F4.wireOp",EDGE,"E666"),sQuery(id+"F4.wireOp",EDGE,"E667"),sQuery(id+"F4.wireOp",EDGE,"E668"),sQuery(id+"F4.wireOp",EDGE,"E669"),sQuery(id+"F4.wireOp",EDGE,"E670"),sQuery(id+"F4.wireOp",EDGE,"E671"),sQuery(id+"F4.wireOp",EDGE,"E672"),sQuery(id+"F4.wireOp",EDGE,"E673"),sQuery(id+"F4.wireOp",EDGE,"E674"),sQuery(id+"F4.wireOp",EDGE,"E675"),sQuery(id+"F4.wireOp",EDGE,"E676"),sQuery(id+"F4.wireOp",EDGE,"E677"),sQuery(id+"F4.wireOp",EDGE,"E678"),sQuery(id+"F4.wireOp",EDGE,"E679"),sQuery(id+"F4.wireOp",EDGE,"E680"),sQuery(id+"F4.wireOp",EDGE,"E681"),sQuery(id+"F4.wireOp",EDGE,"E682"),sQuery(id+"F4.wireOp",EDGE,"E683"),sQuery(id+"F4.wireOp",EDGE,"E684"),sQuery(id+"F4.wireOp",EDGE,"E685"),sQuery(id+"F4.wireOp",EDGE,"E686"),sQuery(id+"F4.wireOp",EDGE,"E687"),sQuery(id+"F4.wireOp",EDGE,"E688"),sQuery(id+"F4.wireOp",EDGE,"E689"),sQuery(id+"F4.wireOp",EDGE,"E690"),sQuery(id+"F4.wireOp",EDGE,"E691"),sQuery(id+"F4.wireOp",EDGE,"E692"),sQuery(id+"F4.wireOp",EDGE,"E693"),sQuery(id+"F4.wireOp",EDGE,"E694"),sQuery(id+"F4.wireOp",EDGE,"E695"),sQuery(id+"F4.wireOp",EDGE,"E696"),sQuery(id+"F4.wireOp",EDGE,"E697"),sQuery(id+"F4.wireOp",EDGE,"E698"),sQuery(id+"F4.wireOp",EDGE,"E699"),sQuery(id+"F4.wireOp",EDGE,"E700"),sQuery(id+"F4.wireOp",EDGE,"E701"),sQuery(id+"F4.wireOp",EDGE,"E702"),sQuery(id+"F4.wireOp",EDGE,"E703"),sQuery(id+"F4.wireOp",EDGE,"E704")])],"isStart":true});
            var sketch = newSketch(context, id + "F6", { "sketchPlane" : qUnion([Q0])});
            skCircle(sketch, "E705.0", {"center": v(0, 6) * mm, "radius": 1 * mm});
            skCircle(sketch, "E706.0", {"center": v(4.24, 4.24) * mm, "radius": 1 * mm});
            skCircle(sketch, "E707.0", {"center": v(6, 0) * mm, "radius": 1 * mm});
            skCircle(sketch, "E708.0", {"center": v(-4.24, 4.24) * mm, "radius": 1 * mm});
            skCircle(sketch, "E709.0", {"center": v(-6, 0) * mm, "radius": 1 * mm});
            skCircle(sketch, "E710.0", {"center": v(0, 0) * mm, "radius": 4.5 * mm});
            skCircle(sketch, "E711.0", {"center": v(-4.24, -4.24) * mm, "radius": 1 * mm});
            skCircle(sketch, "E712.0", {"center": v(0, -6) * mm, "radius": 1 * mm});
            skCircle(sketch, "E713.0", {"center": v(4.24, -4.24) * mm, "radius": 1 * mm});
            skSolve(sketch);
        }
        {
            var Q0;
            Q0 = qSketchRegion(id + "F6", true);
            extrude(context, id + "F7", {"entities" : qUnion([Q0]), "operationType" : NewBodyOperationType.REMOVE, "endBound" : BoundingType.UP_TO_NEXT, "oppositeDirection" : true, "depth" : 25 * mm, "offsetDistance" : 25 * mm});
        }
        {
            var Q0;
            Q0=makeQuery(id+"F5.opExtrude","CAP_FACE",FACE,{"disambiguationData":[OSD([sQuery(id+"F4.wireOp",EDGE,"E285"),sQuery(id+"F4.wireOp",EDGE,"E286"),sQuery(id+"F4.wireOp",EDGE,"E287"),sQuery(id+"F4.wireOp",EDGE,"E288"),sQuery(id+"F4.wireOp",EDGE,"E289"),sQuery(id+"F4.wireOp",EDGE,"E290"),sQuery(id+"F4.wireOp",EDGE,"E291"),sQuery(id+"F4.wireOp",EDGE,"E292"),sQuery(id+"F4.wireOp",EDGE,"E293"),sQuery(id+"F4.wireOp",EDGE,"E294"),sQuery(id+"F4.wireOp",EDGE,"E295"),sQuery(id+"F4.wireOp",EDGE,"E296"),sQuery(id+"F4.wireOp",EDGE,"E297"),sQuery(id+"F4.wireOp",EDGE,"E298"),sQuery(id+"F4.wireOp",EDGE,"E299"),sQuery(id+"F4.wireOp",EDGE,"E300"),sQuery(id+"F4.wireOp",EDGE,"E301"),sQuery(id+"F4.wireOp",EDGE,"E302"),sQuery(id+"F4.wireOp",EDGE,"E303"),sQuery(id+"F4.wireOp",EDGE,"E304"),sQuery(id+"F4.wireOp",EDGE,"E305"),sQuery(id+"F4.wireOp",EDGE,"E306"),sQuery(id+"F4.wireOp",EDGE,"E307"),sQuery(id+"F4.wireOp",EDGE,"E308"),sQuery(id+"F4.wireOp",EDGE,"E309"),sQuery(id+"F4.wireOp",EDGE,"E310"),sQuery(id+"F4.wireOp",EDGE,"E311"),sQuery(id+"F4.wireOp",EDGE,"E312"),sQuery(id+"F4.wireOp",EDGE,"E313"),sQuery(id+"F4.wireOp",EDGE,"E314"),sQuery(id+"F4.wireOp",EDGE,"E315"),sQuery(id+"F4.wireOp",EDGE,"E316"),sQuery(id+"F4.wireOp",EDGE,"E317"),sQuery(id+"F4.wireOp",EDGE,"E318"),sQuery(id+"F4.wireOp",EDGE,"E319"),sQuery(id+"F4.wireOp",EDGE,"E320"),sQuery(id+"F4.wireOp",EDGE,"E321"),sQuery(id+"F4.wireOp",EDGE,"E322"),sQuery(id+"F4.wireOp",EDGE,"E323"),sQuery(id+"F4.wireOp",EDGE,"E324"),sQuery(id+"F4.wireOp",EDGE,"E325"),sQuery(id+"F4.wireOp",EDGE,"E326"),sQuery(id+"F4.wireOp",EDGE,"E327"),sQuery(id+"F4.wireOp",EDGE,"E328"),sQuery(id+"F4.wireOp",EDGE,"E329"),sQuery(id+"F4.wireOp",EDGE,"E330"),sQuery(id+"F4.wireOp",EDGE,"E331"),sQuery(id+"F4.wireOp",EDGE,"E332"),sQuery(id+"F4.wireOp",EDGE,"E333"),sQuery(id+"F4.wireOp",EDGE,"E334"),sQuery(id+"F4.wireOp",EDGE,"E335"),sQuery(id+"F4.wireOp",EDGE,"E336"),sQuery(id+"F4.wireOp",EDGE,"E337"),sQuery(id+"F4.wireOp",EDGE,"E338"),sQuery(id+"F4.wireOp",EDGE,"E339"),sQuery(id+"F4.wireOp",EDGE,"E340"),sQuery(id+"F4.wireOp",EDGE,"E341"),sQuery(id+"F4.wireOp",EDGE,"E342"),sQuery(id+"F4.wireOp",EDGE,"E343"),sQuery(id+"F4.wireOp",EDGE,"E344"),sQuery(id+"F4.wireOp",EDGE,"E345"),sQuery(id+"F4.wireOp",EDGE,"E346"),sQuery(id+"F4.wireOp",EDGE,"E347"),sQuery(id+"F4.wireOp",EDGE,"E348"),sQuery(id+"F4.wireOp",EDGE,"E349"),sQuery(id+"F4.wireOp",EDGE,"E350"),sQuery(id+"F4.wireOp",EDGE,"E351"),sQuery(id+"F4.wireOp",EDGE,"E352"),sQuery(id+"F4.wireOp",EDGE,"E353"),sQuery(id+"F4.wireOp",EDGE,"E354"),sQuery(id+"F4.wireOp",EDGE,"E355"),sQuery(id+"F4.wireOp",EDGE,"E356"),sQuery(id+"F4.wireOp",EDGE,"E357"),sQuery(id+"F4.wireOp",EDGE,"E358"),sQuery(id+"F4.wireOp",EDGE,"E359"),sQuery(id+"F4.wireOp",EDGE,"E360"),sQuery(id+"F4.wireOp",EDGE,"E361"),sQuery(id+"F4.wireOp",EDGE,"E362"),sQuery(id+"F4.wireOp",EDGE,"E363"),sQuery(id+"F4.wireOp",EDGE,"E364"),sQuery(id+"F4.wireOp",EDGE,"E365"),sQuery(id+"F4.wireOp",EDGE,"E366"),sQuery(id+"F4.wireOp",EDGE,"E367"),sQuery(id+"F4.wireOp",EDGE,"E368"),sQuery(id+"F4.wireOp",EDGE,"E369"),sQuery(id+"F4.wireOp",EDGE,"E370"),sQuery(id+"F4.wireOp",EDGE,"E371"),sQuery(id+"F4.wireOp",EDGE,"E372"),sQuery(id+"F4.wireOp",EDGE,"E373"),sQuery(id+"F4.wireOp",EDGE,"E374"),sQuery(id+"F4.wireOp",EDGE,"E375"),sQuery(id+"F4.wireOp",EDGE,"E376"),sQuery(id+"F4.wireOp",EDGE,"E377"),sQuery(id+"F4.wireOp",EDGE,"E378"),sQuery(id+"F4.wireOp",EDGE,"E379"),sQuery(id+"F4.wireOp",EDGE,"E380"),sQuery(id+"F4.wireOp",EDGE,"E381"),sQuery(id+"F4.wireOp",EDGE,"E382"),sQuery(id+"F4.wireOp",EDGE,"E383"),sQuery(id+"F4.wireOp",EDGE,"E384"),sQuery(id+"F4.wireOp",EDGE,"E385"),sQuery(id+"F4.wireOp",EDGE,"E386"),sQuery(id+"F4.wireOp",EDGE,"E387"),sQuery(id+"F4.wireOp",EDGE,"E388"),sQuery(id+"F4.wireOp",EDGE,"E389"),sQuery(id+"F4.wireOp",EDGE,"E390"),sQuery(id+"F4.wireOp",EDGE,"E391"),sQuery(id+"F4.wireOp",EDGE,"E392"),sQuery(id+"F4.wireOp",EDGE,"E393"),sQuery(id+"F4.wireOp",EDGE,"E394"),sQuery(id+"F4.wireOp",EDGE,"E395"),sQuery(id+"F4.wireOp",EDGE,"E396"),sQuery(id+"F4.wireOp",EDGE,"E397"),sQuery(id+"F4.wireOp",EDGE,"E398"),sQuery(id+"F4.wireOp",EDGE,"E399"),sQuery(id+"F4.wireOp",EDGE,"E400"),sQuery(id+"F4.wireOp",EDGE,"E401"),sQuery(id+"F4.wireOp",EDGE,"E402"),sQuery(id+"F4.wireOp",EDGE,"E403"),sQuery(id+"F4.wireOp",EDGE,"E404"),sQuery(id+"F4.wireOp",EDGE,"E405"),sQuery(id+"F4.wireOp",EDGE,"E406"),sQuery(id+"F4.wireOp",EDGE,"E407"),sQuery(id+"F4.wireOp",EDGE,"E408"),sQuery(id+"F4.wireOp",EDGE,"E409"),sQuery(id+"F4.wireOp",EDGE,"E410"),sQuery(id+"F4.wireOp",EDGE,"E411"),sQuery(id+"F4.wireOp",EDGE,"E412"),sQuery(id+"F4.wireOp",EDGE,"E413"),sQuery(id+"F4.wireOp",EDGE,"E414"),sQuery(id+"F4.wireOp",EDGE,"E415"),sQuery(id+"F4.wireOp",EDGE,"E416"),sQuery(id+"F4.wireOp",EDGE,"E417"),sQuery(id+"F4.wireOp",EDGE,"E418"),sQuery(id+"F4.wireOp",EDGE,"E419"),sQuery(id+"F4.wireOp",EDGE,"E420"),sQuery(id+"F4.wireOp",EDGE,"E421"),sQuery(id+"F4.wireOp",EDGE,"E422"),sQuery(id+"F4.wireOp",EDGE,"E423"),sQuery(id+"F4.wireOp",EDGE,"E424"),sQuery(id+"F4.wireOp",EDGE,"E425"),sQuery(id+"F4.wireOp",EDGE,"E426"),sQuery(id+"F4.wireOp",EDGE,"E427"),sQuery(id+"F4.wireOp",EDGE,"E428"),sQuery(id+"F4.wireOp",EDGE,"E429"),sQuery(id+"F4.wireOp",EDGE,"E430"),sQuery(id+"F4.wireOp",EDGE,"E431"),sQuery(id+"F4.wireOp",EDGE,"E432"),sQuery(id+"F4.wireOp",EDGE,"E433"),sQuery(id+"F4.wireOp",EDGE,"E434"),sQuery(id+"F4.wireOp",EDGE,"E435"),sQuery(id+"F4.wireOp",EDGE,"E436"),sQuery(id+"F4.wireOp",EDGE,"E437"),sQuery(id+"F4.wireOp",EDGE,"E438"),sQuery(id+"F4.wireOp",EDGE,"E439"),sQuery(id+"F4.wireOp",EDGE,"E440"),sQuery(id+"F4.wireOp",EDGE,"E441"),sQuery(id+"F4.wireOp",EDGE,"E442"),sQuery(id+"F4.wireOp",EDGE,"E443"),sQuery(id+"F4.wireOp",EDGE,"E444"),sQuery(id+"F4.wireOp",EDGE,"E445"),sQuery(id+"F4.wireOp",EDGE,"E446"),sQuery(id+"F4.wireOp",EDGE,"E447"),sQuery(id+"F4.wireOp",EDGE,"E448"),sQuery(id+"F4.wireOp",EDGE,"E449"),sQuery(id+"F4.wireOp",EDGE,"E450"),sQuery(id+"F4.wireOp",EDGE,"E451"),sQuery(id+"F4.wireOp",EDGE,"E452"),sQuery(id+"F4.wireOp",EDGE,"E453"),sQuery(id+"F4.wireOp",EDGE,"E454"),sQuery(id+"F4.wireOp",EDGE,"E455"),sQuery(id+"F4.wireOp",EDGE,"E456"),sQuery(id+"F4.wireOp",EDGE,"E457"),sQuery(id+"F4.wireOp",EDGE,"E458"),sQuery(id+"F4.wireOp",EDGE,"E459"),sQuery(id+"F4.wireOp",EDGE,"E460"),sQuery(id+"F4.wireOp",EDGE,"E461"),sQuery(id+"F4.wireOp",EDGE,"E462"),sQuery(id+"F4.wireOp",EDGE,"E463"),sQuery(id+"F4.wireOp",EDGE,"E464"),sQuery(id+"F4.wireOp",EDGE,"E465"),sQuery(id+"F4.wireOp",EDGE,"E466"),sQuery(id+"F4.wireOp",EDGE,"E467"),sQuery(id+"F4.wireOp",EDGE,"E468"),sQuery(id+"F4.wireOp",EDGE,"E469"),sQuery(id+"F4.wireOp",EDGE,"E470"),sQuery(id+"F4.wireOp",EDGE,"E471"),sQuery(id+"F4.wireOp",EDGE,"E472"),sQuery(id+"F4.wireOp",EDGE,"E473"),sQuery(id+"F4.wireOp",EDGE,"E474"),sQuery(id+"F4.wireOp",EDGE,"E475"),sQuery(id+"F4.wireOp",EDGE,"E476"),sQuery(id+"F4.wireOp",EDGE,"E477"),sQuery(id+"F4.wireOp",EDGE,"E478"),sQuery(id+"F4.wireOp",EDGE,"E479"),sQuery(id+"F4.wireOp",EDGE,"E480"),sQuery(id+"F4.wireOp",EDGE,"E481"),sQuery(id+"F4.wireOp",EDGE,"E482"),sQuery(id+"F4.wireOp",EDGE,"E483"),sQuery(id+"F4.wireOp",EDGE,"E484"),sQuery(id+"F4.wireOp",EDGE,"E485"),sQuery(id+"F4.wireOp",EDGE,"E486"),sQuery(id+"F4.wireOp",EDGE,"E487"),sQuery(id+"F4.wireOp",EDGE,"E488"),sQuery(id+"F4.wireOp",EDGE,"E489"),sQuery(id+"F4.wireOp",EDGE,"E490"),sQuery(id+"F4.wireOp",EDGE,"E491"),sQuery(id+"F4.wireOp",EDGE,"E492"),sQuery(id+"F4.wireOp",EDGE,"E493"),sQuery(id+"F4.wireOp",EDGE,"E494"),sQuery(id+"F4.wireOp",EDGE,"E495"),sQuery(id+"F4.wireOp",EDGE,"E496"),sQuery(id+"F4.wireOp",EDGE,"E497"),sQuery(id+"F4.wireOp",EDGE,"E498"),sQuery(id+"F4.wireOp",EDGE,"E499"),sQuery(id+"F4.wireOp",EDGE,"E500"),sQuery(id+"F4.wireOp",EDGE,"E501"),sQuery(id+"F4.wireOp",EDGE,"E502"),sQuery(id+"F4.wireOp",EDGE,"E503"),sQuery(id+"F4.wireOp",EDGE,"E504"),sQuery(id+"F4.wireOp",EDGE,"E505"),sQuery(id+"F4.wireOp",EDGE,"E506"),sQuery(id+"F4.wireOp",EDGE,"E507"),sQuery(id+"F4.wireOp",EDGE,"E508"),sQuery(id+"F4.wireOp",EDGE,"E509"),sQuery(id+"F4.wireOp",EDGE,"E510"),sQuery(id+"F4.wireOp",EDGE,"E511"),sQuery(id+"F4.wireOp",EDGE,"E512"),sQuery(id+"F4.wireOp",EDGE,"E513"),sQuery(id+"F4.wireOp",EDGE,"E514"),sQuery(id+"F4.wireOp",EDGE,"E515"),sQuery(id+"F4.wireOp",EDGE,"E516"),sQuery(id+"F4.wireOp",EDGE,"E517"),sQuery(id+"F4.wireOp",EDGE,"E518"),sQuery(id+"F4.wireOp",EDGE,"E519"),sQuery(id+"F4.wireOp",EDGE,"E520"),sQuery(id+"F4.wireOp",EDGE,"E521"),sQuery(id+"F4.wireOp",EDGE,"E522"),sQuery(id+"F4.wireOp",EDGE,"E523"),sQuery(id+"F4.wireOp",EDGE,"E524"),sQuery(id+"F4.wireOp",EDGE,"E525"),sQuery(id+"F4.wireOp",EDGE,"E526"),sQuery(id+"F4.wireOp",EDGE,"E527"),sQuery(id+"F4.wireOp",EDGE,"E528"),sQuery(id+"F4.wireOp",EDGE,"E529"),sQuery(id+"F4.wireOp",EDGE,"E530"),sQuery(id+"F4.wireOp",EDGE,"E531"),sQuery(id+"F4.wireOp",EDGE,"E532"),sQuery(id+"F4.wireOp",EDGE,"E533"),sQuery(id+"F4.wireOp",EDGE,"E534"),sQuery(id+"F4.wireOp",EDGE,"E535"),sQuery(id+"F4.wireOp",EDGE,"E536"),sQuery(id+"F4.wireOp",EDGE,"E537"),sQuery(id+"F4.wireOp",EDGE,"E538"),sQuery(id+"F4.wireOp",EDGE,"E539"),sQuery(id+"F4.wireOp",EDGE,"E540"),sQuery(id+"F4.wireOp",EDGE,"E541"),sQuery(id+"F4.wireOp",EDGE,"E542"),sQuery(id+"F4.wireOp",EDGE,"E543"),sQuery(id+"F4.wireOp",EDGE,"E544"),sQuery(id+"F4.wireOp",EDGE,"E545"),sQuery(id+"F4.wireOp",EDGE,"E546"),sQuery(id+"F4.wireOp",EDGE,"E547"),sQuery(id+"F4.wireOp",EDGE,"E548"),sQuery(id+"F4.wireOp",EDGE,"E549"),sQuery(id+"F4.wireOp",EDGE,"E550"),sQuery(id+"F4.wireOp",EDGE,"E551"),sQuery(id+"F4.wireOp",EDGE,"E552"),sQuery(id+"F4.wireOp",EDGE,"E553"),sQuery(id+"F4.wireOp",EDGE,"E554"),sQuery(id+"F4.wireOp",EDGE,"E555"),sQuery(id+"F4.wireOp",EDGE,"E556"),sQuery(id+"F4.wireOp",EDGE,"E557"),sQuery(id+"F4.wireOp",EDGE,"E558"),sQuery(id+"F4.wireOp",EDGE,"E559"),sQuery(id+"F4.wireOp",EDGE,"E560"),sQuery(id+"F4.wireOp",EDGE,"E561"),sQuery(id+"F4.wireOp",EDGE,"E562"),sQuery(id+"F4.wireOp",EDGE,"E563"),sQuery(id+"F4.wireOp",EDGE,"E564"),sQuery(id+"F4.wireOp",EDGE,"E565"),sQuery(id+"F4.wireOp",EDGE,"E566"),sQuery(id+"F4.wireOp",EDGE,"E567"),sQuery(id+"F4.wireOp",EDGE,"E568"),sQuery(id+"F4.wireOp",EDGE,"E569"),sQuery(id+"F4.wireOp",EDGE,"E570"),sQuery(id+"F4.wireOp",EDGE,"E571"),sQuery(id+"F4.wireOp",EDGE,"E572"),sQuery(id+"F4.wireOp",EDGE,"E573"),sQuery(id+"F4.wireOp",EDGE,"E574"),sQuery(id+"F4.wireOp",EDGE,"E575"),sQuery(id+"F4.wireOp",EDGE,"E576"),sQuery(id+"F4.wireOp",EDGE,"E577"),sQuery(id+"F4.wireOp",EDGE,"E578"),sQuery(id+"F4.wireOp",EDGE,"E579"),sQuery(id+"F4.wireOp",EDGE,"E580"),sQuery(id+"F4.wireOp",EDGE,"E581"),sQuery(id+"F4.wireOp",EDGE,"E582"),sQuery(id+"F4.wireOp",EDGE,"E583"),sQuery(id+"F4.wireOp",EDGE,"E584"),sQuery(id+"F4.wireOp",EDGE,"E585"),sQuery(id+"F4.wireOp",EDGE,"E586"),sQuery(id+"F4.wireOp",EDGE,"E587"),sQuery(id+"F4.wireOp",EDGE,"E588"),sQuery(id+"F4.wireOp",EDGE,"E589"),sQuery(id+"F4.wireOp",EDGE,"E590"),sQuery(id+"F4.wireOp",EDGE,"E591"),sQuery(id+"F4.wireOp",EDGE,"E592"),sQuery(id+"F4.wireOp",EDGE,"E593"),sQuery(id+"F4.wireOp",EDGE,"E594"),sQuery(id+"F4.wireOp",EDGE,"E595"),sQuery(id+"F4.wireOp",EDGE,"E596"),sQuery(id+"F4.wireOp",EDGE,"E597"),sQuery(id+"F4.wireOp",EDGE,"E598"),sQuery(id+"F4.wireOp",EDGE,"E599"),sQuery(id+"F4.wireOp",EDGE,"E600"),sQuery(id+"F4.wireOp",EDGE,"E601"),sQuery(id+"F4.wireOp",EDGE,"E602"),sQuery(id+"F4.wireOp",EDGE,"E603"),sQuery(id+"F4.wireOp",EDGE,"E604"),sQuery(id+"F4.wireOp",EDGE,"E605"),sQuery(id+"F4.wireOp",EDGE,"E606"),sQuery(id+"F4.wireOp",EDGE,"E607"),sQuery(id+"F4.wireOp",EDGE,"E608"),sQuery(id+"F4.wireOp",EDGE,"E609"),sQuery(id+"F4.wireOp",EDGE,"E610"),sQuery(id+"F4.wireOp",EDGE,"E611"),sQuery(id+"F4.wireOp",EDGE,"E612"),sQuery(id+"F4.wireOp",EDGE,"E613"),sQuery(id+"F4.wireOp",EDGE,"E614"),sQuery(id+"F4.wireOp",EDGE,"E615"),sQuery(id+"F4.wireOp",EDGE,"E616"),sQuery(id+"F4.wireOp",EDGE,"E617"),sQuery(id+"F4.wireOp",EDGE,"E618"),sQuery(id+"F4.wireOp",EDGE,"E619"),sQuery(id+"F4.wireOp",EDGE,"E620"),sQuery(id+"F4.wireOp",EDGE,"E621"),sQuery(id+"F4.wireOp",EDGE,"E622"),sQuery(id+"F4.wireOp",EDGE,"E623"),sQuery(id+"F4.wireOp",EDGE,"E624"),sQuery(id+"F4.wireOp",EDGE,"E625"),sQuery(id+"F4.wireOp",EDGE,"E626"),sQuery(id+"F4.wireOp",EDGE,"E627"),sQuery(id+"F4.wireOp",EDGE,"E628"),sQuery(id+"F4.wireOp",EDGE,"E629"),sQuery(id+"F4.wireOp",EDGE,"E630"),sQuery(id+"F4.wireOp",EDGE,"E631"),sQuery(id+"F4.wireOp",EDGE,"E632"),sQuery(id+"F4.wireOp",EDGE,"E633"),sQuery(id+"F4.wireOp",EDGE,"E634"),sQuery(id+"F4.wireOp",EDGE,"E635"),sQuery(id+"F4.wireOp",EDGE,"E636"),sQuery(id+"F4.wireOp",EDGE,"E637"),sQuery(id+"F4.wireOp",EDGE,"E638"),sQuery(id+"F4.wireOp",EDGE,"E639"),sQuery(id+"F4.wireOp",EDGE,"E640"),sQuery(id+"F4.wireOp",EDGE,"E641"),sQuery(id+"F4.wireOp",EDGE,"E642"),sQuery(id+"F4.wireOp",EDGE,"E643"),sQuery(id+"F4.wireOp",EDGE,"E644"),sQuery(id+"F4.wireOp",EDGE,"E645"),sQuery(id+"F4.wireOp",EDGE,"E646"),sQuery(id+"F4.wireOp",EDGE,"E647"),sQuery(id+"F4.wireOp",EDGE,"E648"),sQuery(id+"F4.wireOp",EDGE,"E649"),sQuery(id+"F4.wireOp",EDGE,"E650"),sQuery(id+"F4.wireOp",EDGE,"E651"),sQuery(id+"F4.wireOp",EDGE,"E652"),sQuery(id+"F4.wireOp",EDGE,"E653"),sQuery(id+"F4.wireOp",EDGE,"E654"),sQuery(id+"F4.wireOp",EDGE,"E655"),sQuery(id+"F4.wireOp",EDGE,"E656"),sQuery(id+"F4.wireOp",EDGE,"E657"),sQuery(id+"F4.wireOp",EDGE,"E658"),sQuery(id+"F4.wireOp",EDGE,"E659"),sQuery(id+"F4.wireOp",EDGE,"E660"),sQuery(id+"F4.wireOp",EDGE,"E661"),sQuery(id+"F4.wireOp",EDGE,"E662"),sQuery(id+"F4.wireOp",EDGE,"E663"),sQuery(id+"F4.wireOp",EDGE,"E664"),sQuery(id+"F4.wireOp",EDGE,"E665"),sQuery(id+"F4.wireOp",EDGE,"E666"),sQuery(id+"F4.wireOp",EDGE,"E667"),sQuery(id+"F4.wireOp",EDGE,"E668"),sQuery(id+"F4.wireOp",EDGE,"E669"),sQuery(id+"F4.wireOp",EDGE,"E670"),sQuery(id+"F4.wireOp",EDGE,"E671"),sQuery(id+"F4.wireOp",EDGE,"E672"),sQuery(id+"F4.wireOp",EDGE,"E673"),sQuery(id+"F4.wireOp",EDGE,"E674"),sQuery(id+"F4.wireOp",EDGE,"E675"),sQuery(id+"F4.wireOp",EDGE,"E676"),sQuery(id+"F4.wireOp",EDGE,"E677"),sQuery(id+"F4.wireOp",EDGE,"E678"),sQuery(id+"F4.wireOp",EDGE,"E679"),sQuery(id+"F4.wireOp",EDGE,"E680"),sQuery(id+"F4.wireOp",EDGE,"E681"),sQuery(id+"F4.wireOp",EDGE,"E682"),sQuery(id+"F4.wireOp",EDGE,"E683"),sQuery(id+"F4.wireOp",EDGE,"E684"),sQuery(id+"F4.wireOp",EDGE,"E685"),sQuery(id+"F4.wireOp",EDGE,"E686"),sQuery(id+"F4.wireOp",EDGE,"E687"),sQuery(id+"F4.wireOp",EDGE,"E688"),sQuery(id+"F4.wireOp",EDGE,"E689"),sQuery(id+"F4.wireOp",EDGE,"E690"),sQuery(id+"F4.wireOp",EDGE,"E691"),sQuery(id+"F4.wireOp",EDGE,"E692"),sQuery(id+"F4.wireOp",EDGE,"E693"),sQuery(id+"F4.wireOp",EDGE,"E694"),sQuery(id+"F4.wireOp",EDGE,"E695"),sQuery(id+"F4.wireOp",EDGE,"E696"),sQuery(id+"F4.wireOp",EDGE,"E697"),sQuery(id+"F4.wireOp",EDGE,"E698"),sQuery(id+"F4.wireOp",EDGE,"E699"),sQuery(id+"F4.wireOp",EDGE,"E700"),sQuery(id+"F4.wireOp",EDGE,"E701"),sQuery(id+"F4.wireOp",EDGE,"E702"),sQuery(id+"F4.wireOp",EDGE,"E703"),sQuery(id+"F4.wireOp",EDGE,"E704")])],"isStart":false});
            var sketch = newSketch(context, id + "F8", { "sketchPlane" : qUnion([Q0])});
            skCircle(sketch, "E714", {"center": v(0, 0) * mm, "radius": 9 * mm});
            skSolve(sketch);
        }
        {
            var Q0;
            Q0 = qSketchRegion(id + "F8", true);
            extrude(context, id + "F9", {"entities" : qUnion([Q0]), "operationType" : NewBodyOperationType.REMOVE, "oppositeDirection" : true, "depth" : 2.5 * mm, "offsetDistance" : 25 * mm});
        }
    });
